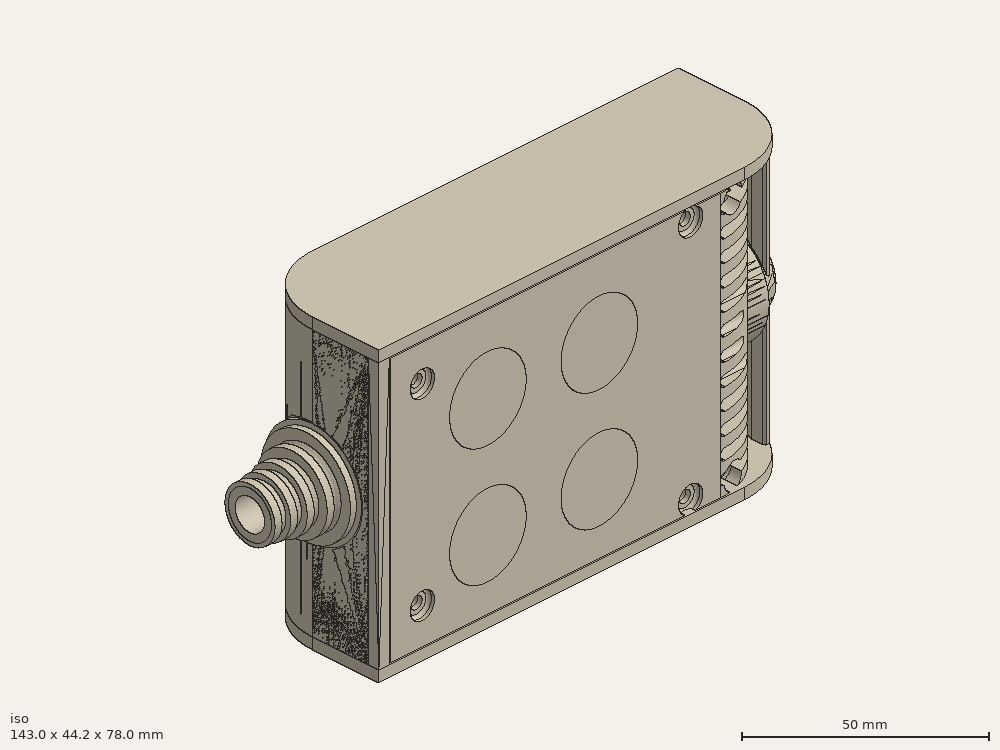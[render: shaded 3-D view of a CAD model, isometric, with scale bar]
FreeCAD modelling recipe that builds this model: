
FCSTD DOCUMENT  (FreeCAD 0.19R0.19.2)
Label: enclosure_128
License: All rights reserved
LicenseURL: http://en.wikipedia.org/wiki/All_rights_reserved
objects: Part::Feature×72, Part::Revolution×72, Part::MultiFuse×61, Sketcher::SketchObject×38, Part::Extrusion×26, Part::Fillet×26, Part::Cut×25, Part::Cylinder×22, Part::Box×12, App::MeasureDistance×4, Part::Chamfer×2
note: 356 computed .brp shape members not serialized (recipe doc carries the construction recipe); baked Part::Feature solids carry a one-line shape summary decoded from their .brp

FEATURE [Sketcher::SketchObject] Sketch  label="topSketch"
  FullyConstrained = true
  sketch-geometry (20):
    g0: LineSegment StartX=5.21097e-06 StartY=3 StartZ=0 EndX=5.21097e-06 EndY=19 EndZ=0
    g1: ArcOfCircle CenterX=19 CenterY=19 CenterZ=0 NormalX=0 NormalY=0 NormalZ=1 AngleXU=0 Radius=19 StartAngle=1.5708 EndAngle=3.14159
    g2: ArcOfCircle CenterX=19 CenterY=19 CenterZ=0 NormalX=0 NormalY=0 NormalZ=1 AngleXU=0 Radius=16 StartAngle=1.5708 EndAngle=3.14159
    g3: LineSegment StartX=114 StartY=35 StartZ=0 EndX=19 EndY=35 EndZ=0
    g4: LineSegment StartX=5.21097e-06 StartY=3 StartZ=0 EndX=5.21097e-06 EndY=0 EndZ=0
    g5: LineSegment StartX=3 StartY=0 StartZ=0 EndX=5.21097e-06 EndY=0 EndZ=0
    g6: LineSegment StartX=3 StartY=19 StartZ=0 EndX=3 EndY=0 EndZ=0
    g7: LineSegment StartX=19 StartY=38 StartZ=0 EndX=124 EndY=38 EndZ=0
    g8: Circle CenterX=119 CenterY=35 CenterZ=0 NormalX=0 NormalY=0 NormalZ=1 AngleXU=0 Radius=1
    g9: Circle CenterX=121 CenterY=35 CenterZ=0 NormalX=0 NormalY=0 NormalZ=1 AngleXU=0 Radius=1
    g10: Circle CenterX=121 CenterY=33 CenterZ=0 NormalX=0 NormalY=0 NormalZ=1 AngleXU=0 Radius=1
    g11: BSplineCurve PolesCount=3 KnotsCount=2 Degree=2 IsPeriodic=0
    g12: GeomPoint X=119 Y=35 Z=0
    g13: GeomPoint X=121 Y=33 Z=0
    g14: LineSegment StartX=119 StartY=35 StartZ=0 EndX=114 EndY=35 EndZ=0
    g15: ArcOfCircle CenterX=105 CenterY=19 CenterZ=0 NormalX=0 NormalY=0 NormalZ=1 AngleXU=0 Radius=19 StartAngle=5.7297 EndAngle=6.28319
    g16: ArcOfCircle CenterX=105 CenterY=19 CenterZ=0 NormalX=0 NormalY=0 NormalZ=1 AngleXU=0 Radius=16 StartAngle=5.60905 EndAngle=6.28319
    g17: LineSegment StartX=121 StartY=33 StartZ=0 EndX=121 EndY=19 EndZ=0
    g18: LineSegment StartX=124 StartY=38 StartZ=0 EndX=124 EndY=19 EndZ=0
    g19: LineSegment StartX=117.5 StartY=9.01251 StartZ=0 EndX=121.163 EndY=9.0125 EndZ=0
  constraints (46):
    c: Vertical(g0)
    c: Block(g0)
    c: Coincident(g1,g0)
    c: Block(g1)
    c: Coincident(g2,g1)
    c: Block(g2)
    c: Coincident(g3,g2)
    c: Horizontal(g3)
    c: Tangent(g3,g2)
    c: Coincident(g4,g0)
    c: Distance(g4) = 3
    c: Vertical(g4)
    c: Coincident(g5,g4)
    c: Horizontal(g5)
    c: Coincident(g6,g2)
    c: Coincident(g6,g5)
    c: Vertical(g6)
    c: Horizontal(g7)
    c: Distance(g7) = 105
    c: Coincident(g7,g1)
    c: Block(g3)
    c: Weight(g8) = 1
    c: Equal(g8,g9)
    c: Equal(g8,g10)
    c: InternalAlignment(g8,g11)
    c: InternalAlignment(g9,g11)
    c: InternalAlignment(g10,g11)
    c: InternalAlignment(g12,g11)
    c: InternalAlignment(g13,g11)
    c: Block(g11)
    c: Coincident(g14,g11)
    c: Coincident(g14,g3)
    c: Horizontal(g14)
    c: Block(g15)
    c: Coincident(g16,g15)
    c: Block(g16)
    c: Coincident(g17,g11)
    c: Coincident(g17,g16)
    c: Vertical(g17)
    c: Distance(g17) = 14
    c: Coincident(g18,g7)
    c: Coincident(g18,g15)
    c: Vertical(g18)
    c: Distance(g18) = 19
    c: Coincident(g19,g16)
    c: Coincident(g19,g15)
FEATURE [Sketcher::SketchObject] Sketch001  label="bottomSketch"
  FullyConstrained = true
  sketch-geometry (32):
    g0: LineSegment StartX=3.3 StartY=-6.03275e-07 StartZ=0 EndX=98 EndY=-6.03275e-07 EndZ=0
    g1: ArcOfCircle CenterX=98 CenterY=19 CenterZ=0 NormalX=0 NormalY=0 NormalZ=1 AngleXU=0 Radius=19 StartAngle=4.71239 EndAngle=5.71103
    g2: LineSegment StartX=6.3 StartY=8 StartZ=0 EndX=3.3 EndY=8 EndZ=0
    g3: LineSegment StartX=3.3 StartY=8 StartZ=0 EndX=3.3 EndY=-6.03275e-07 EndZ=0
    g4: ArcOfCircle CenterX=8.3 CenterY=5 CenterZ=0 NormalX=0 NormalY=0 NormalZ=1 AngleXU=0 Radius=2 StartAngle=3.14159 EndAngle=4.71239
    g5: LineSegment StartX=6.3 StartY=8 StartZ=0 EndX=6.3 EndY=5 EndZ=0
    g6: ArcOfCircle CenterX=98 CenterY=19 CenterZ=0 NormalX=0 NormalY=0 NormalZ=1 AngleXU=0 Radius=12.7 StartAngle=4.71239 EndAngle=6.28319
    g7: LineSegment StartX=94.7 StartY=3 StartZ=0 EndX=8.3 EndY=3 EndZ=0
    g8-g12: Circle x5 (B-spline internal-alignment scaffolding for g13; pole/knot coordinates omitted)
    g13: BSplineCurve PolesCount=5 KnotsCount=3 Degree=3 IsPeriodic=0
    g14: GeomPoint X=98 Y=6.3 Z=0
    g15: GeomPoint X=96.3938 Y=4.71946 Z=0
    g16: GeomPoint X=94.7 Y=3 Z=0
    g17-g23: Circle x7 (B-spline internal-alignment scaffolding for g24; pole/knot coordinates omitted)
    g24: BSplineCurve PolesCount=7 KnotsCount=5 Degree=3 IsPeriodic=0
    g25-g29: GeomPoint x5 (B-spline internal-alignment scaffolding for g24; pole/knot coordinates omitted)
    g30: ArcOfCircle CenterX=98 CenterY=19 CenterZ=0 NormalX=0 NormalY=0 NormalZ=1 AngleXU=0 Radius=15.7 StartAngle=5.81226 EndAngle=6.28319
    g31: LineSegment StartX=110.7 StartY=19 StartZ=0 EndX=113.7 EndY=19 EndZ=0
  constraints (41):
    c: Horizontal(g0)
    c: Coincident(g1,g0)
    c: Block(g1)
    c: Horizontal(g2)
    c: Distance(g2) = 3
    c: Coincident(g3,g2)
    c: Vertical(g3)
    c: Coincident(g3,g0)
    c: Block(g4)
    c: Block(g2)
    c: Coincident(g5,g2)
    c: Coincident(g5,g4)
    c: Vertical(g5)
    c: Coincident(g6,g1)
    c: Block(g6)
    c: Coincident(g7,g4)
    c: Horizontal(g7)
    c: Block(g0)
    c: Block(g7)
    c: Block(g3)
    c: Coincident(g13,g6)
    c: Weight(g8) = 1
    c: Equal(g8, g9-g12) x4
    c: Coincident(g13,g7)
    c: InternalAlignment(g8-g12 -> g13) x5
    c: InternalAlignment(g14,g13)
    c: InternalAlignment(g15,g13)
    c: InternalAlignment(g16,g13)
    c: Block(g13)
    c: Weight(g17) = 1
    c: Equal(g17, g18-g23) x6
    c: Coincident(g24,g1)
    c: InternalAlignment(g17-g23 -> g24) x7
    c: InternalAlignment(g25-g29 -> g24) x5
    c: Block(g24)
    c: Coincident(g30,g24)
    c: Coincident(g31,g6)
    c: Coincident(g31,g30)
    c: Horizontal(g31)
    c: Block(g31)
    c: Block(g30)
FEATURE [Part::Extrusion] Extrude  label="top"
  Base = -> Sketch
  Dir = (0,0,1)
  DirMode = 2
  FaceMakerClass = Part::FaceMakerBullseye
  LengthFwd = 72
  LengthRev = 0
  Solid = true
  Symmetric = false
FEATURE [Part::Extrusion] Extrude001  label="bottom"
  Base = -> Sketch001
  Dir = (0,0,1)
  DirMode = 2
  FaceMakerClass = Part::FaceMakerBullseye
  LengthFwd = 71.4
  LengthRev = 0
  Placement = pos=(0,0,0.3) rot=(0,0,1;0rad)
  Solid = true
  Symmetric = false
FEATURE [Sketcher::SketchObject] Sketch002  label="topSketch001"
  FullyConstrained = true
  sketch-geometry (6):
    g0: ArcOfCircle CenterX=19 CenterY=19 CenterZ=0 NormalX=0 NormalY=0 NormalZ=1 AngleXU=0 Radius=19 StartAngle=1.5708 EndAngle=3.14159
    g1: LineSegment StartX=5.22862e-06 StartY=19 StartZ=0 EndX=5.22862e-06 EndY=1.19904e-11 EndZ=0
    g2: LineSegment StartX=19 StartY=38 StartZ=0 EndX=124 EndY=38 EndZ=0
    g3: LineSegment StartX=5.22862e-06 StartY=1.19904e-11 StartZ=0 EndX=105 EndY=1.19904e-11 EndZ=0
    g4: ArcOfCircle CenterX=105 CenterY=19 CenterZ=0 NormalX=0 NormalY=0 NormalZ=1 AngleXU=0 Radius=19 StartAngle=4.71239 EndAngle=6.28319
    g5: LineSegment StartX=124 StartY=38 StartZ=0 EndX=124 EndY=19 EndZ=0
  constraints (16):
    c: Block(g0)
    c: Coincident(g1,g0)
    c: Vertical(g1)
    c: Horizontal(g2)
    c: Distance(g2) = 105
    c: Coincident(g2,g0)
    c: Distance(g1) = 19
    c: Coincident(g3,g1)
    c: Horizontal(g3)
    c: Distance(g3) = 105
    c: Block(g4)
    c: Coincident(g4,g3)
    c: Coincident(g5,g2)
    c: Coincident(g5,g4)
    c: Vertical(g5)
    c: Distance(g5) = 19
FEATURE [Part::Extrusion] Extrude002  label="sideA"
  Base = -> Sketch002
  Dir = (0,0,1)
  DirMode = 2
  FaceMakerClass = Part::FaceMakerBullseye
  LengthFwd = 3
  LengthRev = 0
  Placement = pos=(0,0,-3) rot=(0,0,1;0rad)
  Solid = true
  Symmetric = false
FEATURE [Sketcher::SketchObject] Sketch003  label="topSketch002"
  FullyConstrained = true
  sketch-geometry (6):
    g0: LineSegment StartX=19 StartY=38 StartZ=0 EndX=117 EndY=38 EndZ=0
    g1: ArcOfCircle CenterX=19 CenterY=19 CenterZ=0 NormalX=0 NormalY=0 NormalZ=1 AngleXU=0 Radius=19 StartAngle=1.5708 EndAngle=3.14159
    g2: LineSegment StartX=117 StartY=38 StartZ=0 EndX=117 EndY=19 EndZ=0
    g3: LineSegment StartX=98 StartY=1.0161e-12 StartZ=0 EndX=5.22862e-06 EndY=1.0161e-12 EndZ=0
    g4: LineSegment StartX=5.22862e-06 StartY=19 StartZ=0 EndX=5.22862e-06 EndY=1.0161e-12 EndZ=0
    g5: ArcOfCircle CenterX=98 CenterY=19 CenterZ=0 NormalX=0 NormalY=0 NormalZ=1 AngleXU=0 Radius=19 StartAngle=4.71239 EndAngle=6.28319
  constraints (16):
    c: Horizontal(g0)
    c: Distance(g0) = 98
    c: Coincident(g1,g0)
    c: Block(g1)
    c: Coincident(g2,g0)
    c: Vertical(g2)
    c: Distance(g2) = 19
    c: Horizontal(g3)
    c: Coincident(g4,g1)
    c: Vertical(g4)
    c: Coincident(g3,g4)
    c: Block(g3)
    c: Coincident(g5,g2)
    c: Coincident(g5,g3)
    c: Block(g0)
    c: Block(g5)
FEATURE [Sketcher::SketchObject] Sketch004
  FullyConstrained = true
  MapMode = 3
  Placement = pos=(0,0,0) rot=(1,0,0;1.5708rad)
  Support = -> [Extrude]
  sketch-geometry (8):
    g0: Circle CenterX=80.351 CenterY=-67.6202 CenterZ=0 NormalX=0 NormalY=0 NormalZ=1 AngleXU=0 Radius=2
    g1: Circle CenterX=80.351 CenterY=-67.6202 CenterZ=0 NormalX=0 NormalY=0 NormalZ=1 AngleXU=0 Radius=3
    g2: Circle CenterX=80.351 CenterY=-4.92017 CenterZ=0 NormalX=0 NormalY=0 NormalZ=1 AngleXU=0 Radius=2
    g3: Circle CenterX=80.351 CenterY=-4.92017 CenterZ=0 NormalX=0 NormalY=0 NormalZ=1 AngleXU=0 Radius=3
    g4: Circle CenterX=23.851 CenterY=-4.92017 CenterZ=0 NormalX=0 NormalY=0 NormalZ=1 AngleXU=0 Radius=2
    g5: Circle CenterX=23.851 CenterY=-4.92017 CenterZ=0 NormalX=0 NormalY=0 NormalZ=1 AngleXU=0 Radius=3
    g6: Circle CenterX=23.851 CenterY=-67.6202 CenterZ=0 NormalX=0 NormalY=0 NormalZ=1 AngleXU=0 Radius=2
    g7: Circle CenterX=23.851 CenterY=-67.6202 CenterZ=0 NormalX=0 NormalY=0 NormalZ=1 AngleXU=0 Radius=3
  constraints (8):
    c: Block(g3)
    c: Block(g2)
    c: Block(g1)
    c: Block(g0)
    c: Block(g6)
    c: Block(g7)
    c: Block(g4)
    c: Block(g5)
FEATURE [Part::Extrusion] Extrude004
  Base = -> Sketch004
  Dir = (0,-1,2e-16)
  DirMode = 2
  FaceMakerClass = Part::FaceMakerBullseye
  LengthFwd = 6
  LengthRev = 0
  Placement = pos=(0,9,0) rot=(0,0,1;0rad)
  Solid = true
  Symmetric = false
FEATURE [Sketcher::SketchObject] Sketch005
  FullyConstrained = true
  MapMode = 3
  Placement = pos=(0,0,0) rot=(1,0,0;1.5708rad)
  Support = -> [Extrude]
  sketch-geometry (8):
    g0: Circle CenterX=80.351 CenterY=-67.6202 CenterZ=0 NormalX=0 NormalY=0 NormalZ=1 AngleXU=0 Radius=3
    g1: Circle CenterX=80.351 CenterY=-4.92017 CenterZ=0 NormalX=0 NormalY=0 NormalZ=1 AngleXU=0 Radius=3
    g2: Circle CenterX=23.851 CenterY=-4.92017 CenterZ=0 NormalX=0 NormalY=0 NormalZ=1 AngleXU=0 Radius=3
    g3: Circle CenterX=23.851 CenterY=-67.6202 CenterZ=0 NormalX=0 NormalY=0 NormalZ=1 AngleXU=0 Radius=3
    g4: Circle CenterX=23.851 CenterY=-67.6202 CenterZ=0 NormalX=0 NormalY=0 NormalZ=1 AngleXU=0 Radius=5
    g5: Circle CenterX=80.351 CenterY=-67.6202 CenterZ=0 NormalX=0 NormalY=0 NormalZ=1 AngleXU=0 Radius=5
    g6: Circle CenterX=23.851 CenterY=-4.92017 CenterZ=0 NormalX=0 NormalY=0 NormalZ=1 AngleXU=0 Radius=5
    g7: Circle CenterX=80.351 CenterY=-4.92017 CenterZ=0 NormalX=0 NormalY=0 NormalZ=1 AngleXU=0 Radius=5
  constraints (8):
    c: Block(g1)
    c: Block(g0)
    c: Block(g3)
    c: Block(g2)
    c: Block(g5)
    c: Block(g4)
    c: Block(g6)
    c: Block(g7)
FEATURE [Part::Extrusion] Extrude005
  Base = -> Sketch005
  Dir = (0,-1,2e-16)
  DirMode = 2
  FaceMakerClass = Part::FaceMakerBullseye
  LengthFwd = 2
  LengthRev = 0
  Solid = true
  Symmetric = false
FEATURE [Sketcher::SketchObject] Sketch006
  FullyConstrained = true
  MapMode = 3
  Placement = pos=(0,0,0) rot=(1,0,0;1.5708rad)
  sketch-geometry (8):
    g0: Circle CenterX=80.351 CenterY=-67.6202 CenterZ=0 NormalX=0 NormalY=0 NormalZ=1 AngleXU=0 Radius=3
    g1: Circle CenterX=80.351 CenterY=-4.92017 CenterZ=0 NormalX=0 NormalY=0 NormalZ=1 AngleXU=0 Radius=3
    g2: Circle CenterX=23.851 CenterY=-4.92017 CenterZ=0 NormalX=0 NormalY=0 NormalZ=1 AngleXU=0 Radius=3
    g3: Circle CenterX=23.851 CenterY=-67.6202 CenterZ=0 NormalX=0 NormalY=0 NormalZ=1 AngleXU=0 Radius=3
    g4: Circle CenterX=23.851 CenterY=-67.6202 CenterZ=0 NormalX=0 NormalY=0 NormalZ=1 AngleXU=0 Radius=5
    g5: Circle CenterX=80.351 CenterY=-67.6202 CenterZ=0 NormalX=0 NormalY=0 NormalZ=1 AngleXU=0 Radius=5
    g6: Circle CenterX=23.851 CenterY=-4.92017 CenterZ=0 NormalX=0 NormalY=0 NormalZ=1 AngleXU=0 Radius=5
    g7: Circle CenterX=80.351 CenterY=-4.92017 CenterZ=0 NormalX=0 NormalY=0 NormalZ=1 AngleXU=0 Radius=5
  constraints (8):
    c: Block(g1)
    c: Block(g0)
    c: Block(g3)
    c: Block(g2)
    c: Block(g5)
    c: Block(g4)
    c: Block(g6)
    c: Block(g7)
FEATURE [Part::Extrusion] Extrude007
  Base = -> Sketch006
  Dir = (0,-1,2e-16)
  DirMode = 2
  FaceMakerClass = Part::FaceMakerBullseye
  LengthFwd = 2
  LengthRev = 0
  Solid = true
  Symmetric = false
FEATURE [Part::Fillet] Fillet
  Base = -> Extrude007
  Edges = 4 edges r=1.99: [Edge6,Edge12,Edge18,Edge24]
FEATURE [Part::Cut] Cut
  Base = -> Extrude005
  Placement = pos=(0,5,0) rot=(0,0,1;0rad)
  Tool = -> Fillet
FEATURE [Part::MultiFuse] Fusion  label="pCBScrews"
  Placement = pos=(-2.5,0,72.3) rot=(0,0,1;0rad)
  Shapes = -> [Extrude004,Cut]
FEATURE [App::MeasureDistance] Distance  label="Distance: 0.69 mm"
  Distance = 0.685967
  P1 = (24.0138,2.9647,0.3)
  P2 = (23.8901,3,-0.373787)
FEATURE [App::MeasureDistance] Distance001  label="Distance: 0.53 mm"
  Distance = 0.533607
  P1 = (80.2939,3,72.2334)
  P2 = (80.281,2.99661,71.7)
FEATURE [Part::Fillet] Fillet001
  Base = -> Extrude001
  Edges = 1 edges r=2.4: [Edge17]
FEATURE [Part::Fillet] Fillet002  label="bottom001"
  Base = -> Fillet001
  Edges = 1 edges r=2.4: [Edge36]
FEATURE [Part::Fillet] Fillet003  label="top001"
  Base = -> Extrude
  Edges = 1 edges r=2: [Edge1]
FEATURE [Sketcher::SketchObject] Sketch007
  FullyConstrained = true
  sketch-geometry (16):
    g0: LineSegment StartX=4 StartY=0 StartZ=0 EndX=4 EndY=2.4 EndZ=0
    g1: LineSegment StartX=4 StartY=2.4 StartZ=0 EndX=7 EndY=2.4 EndZ=0
    g2: LineSegment StartX=4 StartY=0 StartZ=0 EndX=5.7 EndY=0 EndZ=0
    g3: LineSegment StartX=5.7 StartY=0 StartZ=0 EndX=5.7 EndY=-5.6 EndZ=0
    g4-g8: Circle x5 (B-spline internal-alignment scaffolding for g9; pole/knot coordinates omitted)
    g9: BSplineCurve PolesCount=5 KnotsCount=3 Degree=3 IsPeriodic=0
    g10: GeomPoint X=7 Y=2.4 Z=0
    g11: GeomPoint X=10.4582 Y=-1.55472 Z=0
    g12: GeomPoint X=14 Y=-5.6 Z=0
    g13: LineSegment StartX=14 StartY=-5.6 StartZ=0 EndX=14 EndY=-14.1 EndZ=0
    g14: LineSegment StartX=14 StartY=-14.1 StartZ=0 EndX=6.5 EndY=-14.1 EndZ=0
    g15: LineSegment StartX=5.7 StartY=-5.6 StartZ=0 EndX=6.5 EndY=-14.1 EndZ=0
  constraints (28):
    c: Distance(g0) = 2.4
    c: Vertical(g0)
    c: Block(g0)
    c: Coincident(g1,g0)
    c: Horizontal(g1)
    c: Distance(g1) = 3
    c: Coincident(g2,g0)
    c: Horizontal(g2)
    c: Distance(g2) = 1.7
    c: Coincident(g3,g2)
    c: Vertical(g3)
    c: Distance(g3) = 5.6
    c: Coincident(g9,g1)
    c: Weight(g4) = 1
    c: Equal(g4, g5-g8) x4
    c: InternalAlignment(g4-g8 -> g9) x5
    c: InternalAlignment(g10,g9)
    c: InternalAlignment(g11,g9)
    c: InternalAlignment(g12,g9)
    c: Block(g9)
    c: Coincident(g13,g9)
    c: Vertical(g13)
    c: Distance(g13) = 8.5
    c: Coincident(g14,g13)
    c: Horizontal(g14)
    c: Distance(g14) = 7.5
    c: Coincident(g15,g3)
    c: Coincident(g15,g14)
FEATURE [Part::Feature] Face
  shape: bbox 10 x 16.5 x 2e-07 mm, 1 faces, 0 solids (baked)
FEATURE [Part::Revolution] Revolve  label="plugHousing"
  Angle = 360
  Axis = (0,1,0)
  Base = (0,0,0)
  FaceMakerClass = Part::FaceMakerBullseye
  Placement = pos=(0,0,36.15) rot=(0,0,1;0rad)
  Solid = false
  Source = -> Face
  Symmetric = false
FEATURE [Part::Feature] Face001
  shape: bbox 10 x 16.5 x 2e-07 mm, 1 faces, 0 solids (baked)
FEATURE [Part::Revolution] Revolve001  label="plugHousing001"
  Angle = 360
  Axis = (0,1,0)
  Base = (0,0,0)
  FaceMakerClass = Part::FaceMakerBullseye
  Placement = pos=(0,0,36.15) rot=(0,0,1;0rad)
  Solid = false
  Source = -> Face001
  Symmetric = false
FEATURE [Part::MultiFuse] Fusion001  label="plugHousing002"
  Placement = pos=(0,0,0) rot=(0,0,1;1.5708rad)
  Shapes = -> [Revolve001,Revolve]
FEATURE [Part::Feature] Face002
  shape: bbox 10 x 16.5 x 2e-07 mm, 1 faces, 0 solids (baked)
FEATURE [Part::Revolution] Revolve003  label="plugHousing005"
  Angle = 360
  Axis = (0,1,0)
  Base = (0,0,0)
  FaceMakerClass = Part::FaceMakerBullseye
  Placement = pos=(0,0,36.15) rot=(0,0,1;0rad)
  Solid = false
  Source = -> Face002
  Symmetric = false
FEATURE [Part::Feature] Face003
  shape: bbox 10 x 16.5 x 2e-07 mm, 1 faces, 0 solids (baked)
FEATURE [Part::Revolution] Revolve002  label="plugHousing003"
  Angle = 360
  Axis = (0,1,0)
  Base = (0,0,0)
  FaceMakerClass = Part::FaceMakerBullseye
  Placement = pos=(0,0,36.15) rot=(0,0,1;0rad)
  Solid = false
  Source = -> Face003
  Symmetric = false
FEATURE [Part::MultiFuse] Fusion002  label="plugHousing004"
  Placement = pos=(0,0,0) rot=(0,0,1;1.5708rad)
  Shapes = -> [Revolve002,Revolve003]
FEATURE [Part::MultiFuse] Fusion003  label="plugHousing006"
  Placement = pos=(0,19,0) rot=(0,0,1;3.14159rad)
  Shapes = -> [Fusion002,Fusion001]
FEATURE [Part::Feature] Face004
  shape: bbox 10 x 16.5 x 2e-07 mm, 1 faces, 0 solids (baked)
FEATURE [Part::Revolution] Revolve006  label="plugHousing010"
  Angle = 360
  Axis = (0,1,0)
  Base = (0,0,0)
  FaceMakerClass = Part::FaceMakerBullseye
  Placement = pos=(0,0,36.15) rot=(0,0,1;0rad)
  Solid = false
  Source = -> Face004
  Symmetric = false
FEATURE [Part::Feature] Face005
  shape: bbox 10 x 16.5 x 2e-07 mm, 1 faces, 0 solids (baked)
FEATURE [Part::Revolution] Revolve007  label="plugHousing011"
  Angle = 360
  Axis = (0,1,0)
  Base = (0,0,0)
  FaceMakerClass = Part::FaceMakerBullseye
  Placement = pos=(0,0,36.15) rot=(0,0,1;0rad)
  Solid = false
  Source = -> Face005
  Symmetric = false
FEATURE [Part::Feature] Face006
  shape: bbox 10 x 16.5 x 2e-07 mm, 1 faces, 0 solids (baked)
FEATURE [Part::Revolution] Revolve004  label="plugHousing007"
  Angle = 360
  Axis = (0,1,0)
  Base = (0,0,0)
  FaceMakerClass = Part::FaceMakerBullseye
  Placement = pos=(0,0,36.15) rot=(0,0,1;0rad)
  Solid = false
  Source = -> Face006
  Symmetric = false
FEATURE [Part::MultiFuse] Fusion004  label="plugHousing009"
  Placement = pos=(0,0,0) rot=(0,0,1;1.5708rad)
  Shapes = -> [Revolve004,Revolve007]
FEATURE [Part::Feature] Face007
  shape: bbox 10 x 16.5 x 2e-07 mm, 1 faces, 0 solids (baked)
FEATURE [Part::Revolution] Revolve005  label="plugHousing008"
  Angle = 360
  Axis = (0,1,0)
  Base = (0,0,0)
  FaceMakerClass = Part::FaceMakerBullseye
  Placement = pos=(0,0,36.15) rot=(0,0,1;0rad)
  Solid = false
  Source = -> Face007
  Symmetric = false
FEATURE [Part::MultiFuse] Fusion005  label="plugHousing012"
  Placement = pos=(0,0,0) rot=(0,0,1;1.5708rad)
  Shapes = -> [Revolve006,Revolve005]
FEATURE [Part::MultiFuse] Fusion006  label="plugHousing013"
  Placement = pos=(0,19,0) rot=(0,0,1;3.14159rad)
  Shapes = -> [Fusion005,Fusion004]
FEATURE [Part::MultiFuse] Fusion007  label="plugHousing014"
  Placement = pos=(122.621,0,-0.15) rot=(0,0,1;0rad)
  Shapes = -> [Fusion003,Fusion006]
FEATURE [Part::Cylinder] Cylinder002
  Angle = 360
  AttacherType = Attacher::AttachEngine3D
  Height = 20
  Placement = pos=(0,0,36.15) rot=(0,0,1;0rad)
  Radius = 4
FEATURE [Part::Cylinder] Cylinder003
  Angle = 360
  AttacherType = Attacher::AttachEngine3D
  Height = 10
  Placement = pos=(0,0,36.15) rot=(0,0,1;0rad)
  Radius = 4
FEATURE [Part::MultiFuse] Fusion009  label="removeToCreateHoleForPlugHousing"
  Placement = pos=(70,19,36.15) rot=(0,1,0;1.5708rad)
  Shapes = -> [Cylinder002,Cylinder003]
FEATURE [Part::Cylinder] Cylinder004
  Angle = 360
  AttacherType = Attacher::AttachEngine3D
  Height = 20
  Placement = pos=(0,0,36.15) rot=(0,0,1;0rad)
  Radius = 4
FEATURE [Part::Cylinder] Cylinder005
  Angle = 360
  AttacherType = Attacher::AttachEngine3D
  Height = 10
  Placement = pos=(0,0,36.15) rot=(0,0,1;0rad)
  Radius = 4
FEATURE [Part::MultiFuse] Fusion010  label="removeToCreateHoleForPlugHousing001"
  Placement = pos=(70,19,36.15) rot=(0,1,0;1.5708rad)
  Shapes = -> [Cylinder004,Cylinder005]
FEATURE [Part::Cut] Cut001
  Base = -> Fillet003
  Tool = -> Fusion010
FEATURE [Part::Cut] Cut002  label="Bottom"
  Base = -> Fillet002
  Tool = -> Fusion009
FEATURE [Part::Feature] Face008
  shape: bbox 10 x 16.5 x 2e-07 mm, 1 faces, 0 solids (baked)
FEATURE [Part::Revolution] Revolve011  label="plugHousing021"
  Angle = 360
  Axis = (0,1,0)
  Base = (0,0,0)
  FaceMakerClass = Part::FaceMakerBullseye
  Placement = pos=(0,0,36.15) rot=(0,0,1;0rad)
  Solid = false
  Source = -> Face008
  Symmetric = false
FEATURE [Part::Feature] Face009
  shape: bbox 10 x 16.5 x 2e-07 mm, 1 faces, 0 solids (baked)
FEATURE [Part::Revolution] Revolve012  label="plugHousing022"
  Angle = 360
  Axis = (0,1,0)
  Base = (0,0,0)
  FaceMakerClass = Part::FaceMakerBullseye
  Placement = pos=(0,0,36.15) rot=(0,0,1;0rad)
  Solid = false
  Source = -> Face009
  Symmetric = false
FEATURE [Part::Feature] Face010 .. Face013  x4 (patterned run collapsed; names and placements below)
  shape: bbox 10 x 16.5 x 2e-07 mm, 1 faces, 0 solids (baked)
FEATURE [Part::Revolution] Revolve015  label="plugHousing027"
  Angle = 360
  Axis = (0,1,0)
  Base = (0,0,0)
  FaceMakerClass = Part::FaceMakerBullseye
  Placement = pos=(0,0,36.15) rot=(0,0,1;0rad)
  Solid = false
  Source = -> Face013
  Symmetric = false
FEATURE [Part::Feature] Face014
  shape: bbox 10 x 16.5 x 2e-07 mm, 1 faces, 0 solids (baked)
FEATURE [Part::Feature] Face015
  shape: bbox 10 x 16.5 x 2e-07 mm, 1 faces, 0 solids (baked)
FEATURE [Part::Feature] Face016
  shape: bbox 10 x 16.5 x 2e-07 mm, 1 faces, 0 solids (baked)
FEATURE [Part::Revolution] Revolve019  label="plugHousing033"
  Angle = 360
  Axis = (0,1,0)
  Base = (0,0,0)
  FaceMakerClass = Part::FaceMakerBullseye
  Placement = pos=(0,0,36.15) rot=(0,0,1;0rad)
  Solid = false
  Source = -> Face016
  Symmetric = false
FEATURE [Part::Feature] Face017
  shape: bbox 10 x 16.5 x 2e-07 mm, 1 faces, 0 solids (baked)
FEATURE [Part::Revolution] Revolve020  label="plugHousing034"
  Angle = 360
  Axis = (0,1,0)
  Base = (0,0,0)
  FaceMakerClass = Part::FaceMakerBullseye
  Placement = pos=(0,0,36.15) rot=(0,0,1;0rad)
  Solid = false
  Source = -> Face017
  Symmetric = false
FEATURE [Part::Feature] Face018
  shape: bbox 10 x 16.5 x 2e-07 mm, 1 faces, 0 solids (baked)
FEATURE [Part::Revolution] Revolve016  label="plugHousing030"
  Angle = 360
  Axis = (0,1,0)
  Base = (0,0,0)
  FaceMakerClass = Part::FaceMakerBullseye
  Placement = pos=(0,0,36.15) rot=(0,0,1;0rad)
  Solid = false
  Source = -> Face018
  Symmetric = false
FEATURE [Part::MultiFuse] Fusion020  label="plugHousing038"
  Placement = pos=(0,0,0) rot=(0,0,1;1.5708rad)
  Shapes = -> [Revolve016,Revolve020]
FEATURE [Part::Feature] Face019
  shape: bbox 10 x 16.5 x 2e-07 mm, 1 faces, 0 solids (baked)
FEATURE [Part::Feature] Face020
  shape: bbox 10 x 16.5 x 2e-07 mm, 1 faces, 0 solids (baked)
FEATURE [Part::Revolution] Revolve017  label="plugHousing031"
  Angle = 360
  Axis = (0,1,0)
  Base = (0,0,0)
  FaceMakerClass = Part::FaceMakerBullseye
  Placement = pos=(0,0,36.15) rot=(0,0,1;0rad)
  Solid = false
  Source = -> Face020
  Symmetric = false
FEATURE [Part::MultiFuse] Fusion021  label="plugHousing039"
  Placement = pos=(0,0,0) rot=(0,0,1;1.5708rad)
  Shapes = -> [Revolve019,Revolve017]
FEATURE [Part::MultiFuse] Fusion023  label="plugHousing041"
  Placement = pos=(0,19,0) rot=(0,0,1;3.14159rad)
  Shapes = -> [Fusion021,Fusion020]
FEATURE [Part::Revolution] Revolve022  label="plugHousing043"
  Angle = 360
  Axis = (0,1,0)
  Base = (0,0,0)
  FaceMakerClass = Part::FaceMakerBullseye
  Placement = pos=(0,0,36.15) rot=(0,0,1;0rad)
  Solid = false
  Source = -> Face019
  Symmetric = false
FEATURE [Part::Feature] Face021
  shape: bbox 10 x 16.5 x 2e-07 mm, 1 faces, 0 solids (baked)
FEATURE [Part::Revolution] Revolve023  label="plugHousing044"
  Angle = 360
  Axis = (0,1,0)
  Base = (0,0,0)
  FaceMakerClass = Part::FaceMakerBullseye
  Placement = pos=(0,0,36.15) rot=(0,0,1;0rad)
  Solid = false
  Source = -> Face021
  Symmetric = false
FEATURE [Part::Feature] Face022
  shape: bbox 10 x 16.5 x 2e-07 mm, 1 faces, 0 solids (baked)
FEATURE [Part::Revolution] Revolve018  label="plugHousing032"
  Angle = 360
  Axis = (0,1,0)
  Base = (0,0,0)
  FaceMakerClass = Part::FaceMakerBullseye
  Placement = pos=(0,0,36.15) rot=(0,0,1;0rad)
  Solid = false
  Source = -> Face022
  Symmetric = false
FEATURE [Part::MultiFuse] Fusion022  label="plugHousing040"
  Placement = pos=(0,0,0) rot=(0,0,1;1.5708rad)
  Shapes = -> [Revolve018,Revolve023]
FEATURE [Part::Feature] Face023
  shape: bbox 10 x 16.5 x 2e-07 mm, 1 faces, 0 solids (baked)
FEATURE [Part::Revolution] Revolve021  label="plugHousing035"
  Angle = 360
  Axis = (0,1,0)
  Base = (0,0,0)
  FaceMakerClass = Part::FaceMakerBullseye
  Placement = pos=(0,0,36.15) rot=(0,0,1;0rad)
  Solid = false
  Source = -> Face023
  Symmetric = false
FEATURE [Part::MultiFuse] Fusion018  label="plugHousing036"
  Placement = pos=(0,0,0) rot=(0,0,1;1.5708rad)
  Shapes = -> [Revolve022,Revolve021]
FEATURE [Part::MultiFuse] Fusion019  label="plugHousing037"
  Placement = pos=(0,19,0) rot=(0,0,1;3.14159rad)
  Shapes = -> [Fusion018,Fusion022]
FEATURE [Part::MultiFuse] Fusion024  label="plugHousing042"
  Placement = pos=(122.621,0,-0.15) rot=(0,0,1;0rad)
  Shapes = -> [Fusion023,Fusion019]
FEATURE [Part::Cylinder] Cylinder006
  Angle = 360
  AttacherType = Attacher::AttachEngine3D
  Height = 20
  Placement = pos=(0,0,36.15) rot=(0,0,1;0rad)
  Radius = 14.3
FEATURE [Part::Cylinder] Cylinder007
  Angle = 360
  AttacherType = Attacher::AttachEngine3D
  Height = 10
  Placement = pos=(0,0,36.15) rot=(0,0,1;0rad)
  Radius = 4
FEATURE [Part::MultiFuse] Fusion026  label="removeToCreteHoleForPlugHousing"
  Placement = pos=(70,19,36) rot=(0,1,0;1.5708rad)
  Shapes = -> [Cylinder006,Cylinder007]
FEATURE [Part::Box] Box001  label="Cube001"
  AttacherType = Attacher::AttachEngine3D
  Height = 28
  Length = 3
  Placement = pos=(110.7,19,22) rot=(0,0,1;0rad)
  Width = 15.7
FEATURE [Part::Cut] Cut003  label="top002"
  Base = -> Cut001
  Tool = -> Fusion007
FEATURE [Part::Revolution] Revolve008  label="plugHousing015"
  Angle = 360
  Axis = (0,1,0)
  Base = (0,0,0)
  FaceMakerClass = Part::FaceMakerBullseye
  Placement = pos=(0,0,36.15) rot=(0,0,1;0rad)
  Solid = false
  Source = -> Face010
  Symmetric = false
FEATURE [Part::MultiFuse] Fusion013  label="plugHousing020"
  Placement = pos=(0,0,0) rot=(0,0,1;1.5708rad)
  Shapes = -> [Revolve008,Revolve012]
FEATURE [Part::Cut] Cut004  label="top003"
  Base = -> Cut003
  Placement = pos=(1,0,0) rot=(0,0,1;0rad)
  Tool = -> Fusion026
FEATURE [Part::Cylinder] Cylinder008
  Angle = 360
  AttacherType = Attacher::AttachEngine3D
  Height = 20
  Placement = pos=(0,0,36.15) rot=(0,0,1;0rad)
  Radius = 10.3
FEATURE [Part::Cylinder] Cylinder009
  Angle = 360
  AttacherType = Attacher::AttachEngine3D
  Height = 10
  Placement = pos=(0,0,36.15) rot=(0,0,1;0rad)
  Radius = 4
FEATURE [Part::MultiFuse] Fusion027  label="removeToCreteHoleForPlugHousing001"
  Placement = pos=(70,19,36) rot=(0,1,0;1.5708rad)
  Shapes = -> [Cylinder008,Cylinder009]
FEATURE [Part::Cut] Cut005  label="plugHousingTab"
  Base = -> Box001
  Tool = -> Fusion027
FEATURE [Part::MultiFuse] Fusion028  label="plugHousing045"
  Shapes = -> [Fusion024,Cut005]
FEATURE [Part::Box] Box002  label="Cube002"
  AttacherType = Attacher::AttachEngine3D
  Height = 28.8
  Length = 3
  Placement = pos=(107.3,28,21.6) rot=(0,0,1;0rad)
  Width = 7
FEATURE [Part::Box] Box003  label="Cube003"
  AttacherType = Attacher::AttachEngine3D
  Height = 3
  Length = 6.4
  Placement = pos=(107.3,28,18.6) rot=(0,0,1;0rad)
  Width = 7
FEATURE [Part::Box] Box004  label="Cube004"
  AttacherType = Attacher::AttachEngine3D
  Height = 3
  Length = 6.4
  Placement = pos=(107.3,28,50.4) rot=(0,0,1;0rad)
  Width = 7
FEATURE [Part::MultiFuse] Fusion029  label="plugHousingBracketHolder"
  Shapes = -> [Box004,Box002,Box003]
FEATURE [Part::Cylinder] Cylinder010
  Angle = 360
  AttacherType = Attacher::AttachEngine3D
  Height = 20
  Placement = pos=(0,0,36.15) rot=(0,0,1;0rad)
  Radius = 14.3
FEATURE [Part::Cylinder] Cylinder011
  Angle = 360
  AttacherType = Attacher::AttachEngine3D
  Height = 10
  Placement = pos=(0,0,36.15) rot=(0,0,1;0rad)
  Radius = 4
FEATURE [Part::MultiFuse] Fusion030  label="removeToCreteHoleForPlugHousing002"
  Placement = pos=(70,19,36) rot=(0,1,0;1.5708rad)
  Shapes = -> [Cylinder010,Cylinder011]
FEATURE [Part::Cut] Cut006  label="plugHousingBracketHolder001"
  Base = -> Fusion029
  Tool = -> Fusion030
FEATURE [Part::Cylinder] Cylinder012
  Angle = 360
  AttacherType = Attacher::AttachEngine3D
  Height = 20
  Placement = pos=(0,0,36.15) rot=(0,0,1;0rad)
  Radius = 7
FEATURE [Part::Cylinder] Cylinder013
  Angle = 360
  AttacherType = Attacher::AttachEngine3D
  Height = 10
  Placement = pos=(0,0,36.15) rot=(0,0,1;0rad)
  Radius = 4
FEATURE [Part::MultiFuse] Fusion032  label="removeToCreteHoleForPlugHousing003"
  Placement = pos=(70,19,36) rot=(0,1,0;1.5708rad)
  Shapes = -> [Cylinder012,Cylinder013]
FEATURE [Part::Cut] Cut007  label="bottom002"
  Base = -> Cut002
  Tool = -> Fusion032
FEATURE [Sketcher::SketchObject] Sketch008
  FullyConstrained = true
  sketch-geometry (54):
    g0: LineSegment StartX=-4.2 StartY=0 StartZ=0 EndX=-6.2 EndY=0 EndZ=0
    g1: LineSegment StartX=-14 StartY=-18 StartZ=0 EndX=-14 EndY=-26.5 EndZ=0
    g2: LineSegment StartX=-4.2 StartY=0 StartZ=0 EndX=-4.2 EndY=-13.4877 EndZ=0
    g3: Circle CenterX=-4.2 CenterY=-13.4877 CenterZ=0 NormalX=0 NormalY=0 NormalZ=1 AngleXU=0 Radius=1
    g4: Circle CenterX=-4.2 CenterY=-26.5 CenterZ=0 NormalX=0 NormalY=0 NormalZ=1 AngleXU=0 Radius=1
    g5: Circle CenterX=-8.2 CenterY=-26.5 CenterZ=0 NormalX=0 NormalY=0 NormalZ=1 AngleXU=0 Radius=1
    g6: BSplineCurve PolesCount=3 KnotsCount=2 Degree=2 IsPeriodic=0
    g7: GeomPoint X=-4.2 Y=-13.4877 Z=0
    g8: GeomPoint X=-8.2 Y=-26.5 Z=0
    g9: LineSegment StartX=-14 StartY=-26.5 StartZ=0 EndX=-8.2 EndY=-26.5 EndZ=0
    g10: LineSegment StartX=-10.15 StartY=-12 StartZ=0 EndX=-10.15 EndY=-14 EndZ=0
    g11: LineSegment StartX=-12.8401 StartY=-16 StartZ=0 EndX=-10.1571 EndY=-16 EndZ=0
    g12: LineSegment StartX=-10.15 StartY=-14 StartZ=0 EndX=-8.70761 EndY=-14 EndZ=0
    g13: LineSegment StartX=-12.8401 StartY=-16 StartZ=0 EndX=-12.8401 EndY=-17.6958 EndZ=0
    g14: LineSegment StartX=-10.15 StartY=-12 StartZ=0 EndX=-7.79258 EndY=-12 EndZ=0
    g15: Circle CenterX=-6.2215 CenterY=-2 CenterZ=0 NormalX=0 NormalY=0 NormalZ=1 AngleXU=0 Radius=1
    g16: Circle CenterX=-6.22762 CenterY=-2.58724 CenterZ=0 NormalX=0 NormalY=0 NormalZ=1 AngleXU=0 Radius=1
    g17: Circle CenterX=-6.32538 CenterY=-4 CenterZ=0 NormalX=0 NormalY=0 NormalZ=1 AngleXU=0 Radius=1
    g18: BSplineCurve PolesCount=3 KnotsCount=2 Degree=2 IsPeriodic=0
    g19: GeomPoint X=-6.2215 Y=-2 Z=0
    g20: GeomPoint X=-6.32538 Y=-4 Z=0
    g21: Circle CenterX=-6.48644 CenterY=-5.99526 CenterZ=0 NormalX=0 NormalY=0 NormalZ=1 AngleXU=0 Radius=1
    g22: Circle CenterX=-6.58486 CenterY=-6.99526 CenterZ=0 NormalX=0 NormalY=0 NormalZ=1 AngleXU=0 Radius=1
    g23: Circle CenterX=-6.77343 CenterY=-8 CenterZ=0 NormalX=0 NormalY=0 NormalZ=1 AngleXU=0 Radius=1
    g24: BSplineCurve PolesCount=3 KnotsCount=2 Degree=2 IsPeriodic=0
    g25: GeomPoint X=-6.48644 Y=-5.99526 Z=0
    g26: GeomPoint X=-6.77343 Y=-8 Z=0
    g27: Circle CenterX=-7.19003 CenterY=-10 CenterZ=0 NormalX=0 NormalY=0 NormalZ=1 AngleXU=0 Radius=1
    g28: Circle CenterX=-7.44407 CenterY=-11.0915 CenterZ=0 NormalX=0 NormalY=0 NormalZ=1 AngleXU=0 Radius=1
    g29: Circle CenterX=-7.79258 CenterY=-12 CenterZ=0 NormalX=0 NormalY=0 NormalZ=1 AngleXU=0 Radius=1
    g30: BSplineCurve PolesCount=3 KnotsCount=2 Degree=2 IsPeriodic=0
    g31: GeomPoint X=-7.19003 Y=-10 Z=0
    g32: GeomPoint X=-7.79258 Y=-12 Z=0
    g33: Circle CenterX=-8.70761 CenterY=-14 CenterZ=0 NormalX=0 NormalY=0 NormalZ=1 AngleXU=0 Radius=1
    g34: Circle CenterX=-9.33087 CenterY=-15.1837 CenterZ=0 NormalX=0 NormalY=0 NormalZ=1 AngleXU=0 Radius=1
    g35: Circle CenterX=-10.1571 CenterY=-16 CenterZ=0 NormalX=0 NormalY=0 NormalZ=1 AngleXU=0 Radius=1
    g36: BSplineCurve PolesCount=3 KnotsCount=2 Degree=2 IsPeriodic=0
    g37: GeomPoint X=-8.70761 Y=-14 Z=0
    g38: GeomPoint X=-10.1571 Y=-16 Z=0
    g39: Circle CenterX=-12.8401 CenterY=-17.6958 CenterZ=0 NormalX=0 NormalY=0 NormalZ=1 AngleXU=0 Radius=1
    g40: Circle CenterX=-13.3521 CenterY=-17.9027 CenterZ=0 NormalX=0 NormalY=0 NormalZ=1 AngleXU=0 Radius=1
    g41: Circle CenterX=-14 CenterY=-18 CenterZ=0 NormalX=0 NormalY=0 NormalZ=1 AngleXU=0 Radius=1
    g42: BSplineCurve PolesCount=3 KnotsCount=2 Degree=2 IsPeriodic=0
    g43: GeomPoint X=-12.8401 Y=-17.6958 Z=0
    g44: GeomPoint X=-14 Y=-18 Z=0
    g45: LineSegment StartX=-6.2 StartY=0 StartZ=0 EndX=-7.2 EndY=0 EndZ=0
    g46: LineSegment StartX=-7.2 StartY=0 StartZ=0 EndX=-7.2 EndY=-2 EndZ=0
    g47: LineSegment StartX=-7.2 StartY=-2 StartZ=0 EndX=-6.2215 EndY=-2 EndZ=0
    g48: LineSegment StartX=-6.32538 StartY=-4 StartZ=0 EndX=-7.65538 EndY=-4 EndZ=0
    g49: LineSegment StartX=-7.65538 StartY=-4 StartZ=0 EndX=-7.65538 EndY=-5.99526 EndZ=0
    g50: LineSegment StartX=-7.65538 StartY=-5.99526 StartZ=0 EndX=-6.48644 EndY=-5.99526 EndZ=0
    g51: LineSegment StartX=-6.77343 StartY=-8 StartZ=0 EndX=-8.43343 EndY=-8 EndZ=0
    g52: LineSegment StartX=-8.43343 StartY=-8 StartZ=0 EndX=-8.43343 EndY=-10 EndZ=0
    g53: LineSegment StartX=-8.43343 StartY=-10 StartZ=0 EndX=-7.19003 EndY=-10 EndZ=0
  constraints (112):
    c: Horizontal(g0)
    c: Distance(g0) = 2
    c: Block(g0)
    c: Vertical(g1)
    c: Coincident(g2,g0)
    c: Vertical(g2)
    c: Block(g2)
    c: Coincident(g6,g2)
    c: Weight(g3) = 1
    c: Equal(g3,g4)
    c: Equal(g3,g5)
    c: InternalAlignment(g3,g6)
    c: InternalAlignment(g4,g6)
    c: InternalAlignment(g5,g6)
    c: InternalAlignment(g7,g6)
    c: InternalAlignment(g8,g6)
    c: Block(g6)
    c: Coincident(g9,g1)
    c: Coincident(g9,g6)
    c: Horizontal(g9)
    c: Vertical(g10)
    c: Block(g10)
    c: Horizontal(g11)
    c: Block(g11)
    c: Coincident(g12,g10)
    c: Horizontal(g12)
    c: Block(g12)
    c: Coincident(g13,g11)
    c: Vertical(g13)
    c: Block(g13)
    c: Coincident(g14,g10)
    c: Horizontal(g14)
    c: Block(g14)
    c: Block(g9)
    c: Block(g1)
    c: Weight(g15) = 1
    c: Equal(g15,g16)
    c: Equal(g15,g17)
    c: InternalAlignment(g15,g18)
    c: InternalAlignment(g16,g18)
    c: InternalAlignment(g17,g18)
    c: InternalAlignment(g19,g18)
    c: InternalAlignment(g20,g18)
    c: Weight(g21) = 1
    c: Equal(g21,g22)
    c: Equal(g21,g23)
    c: InternalAlignment(g21,g24)
    c: InternalAlignment(g22,g24)
    c: InternalAlignment(g23,g24)
    c: InternalAlignment(g25,g24)
    c: InternalAlignment(g26,g24)
    c: Weight(g27) = 1
    c: Equal(g27,g28)
    c: Equal(g27,g29)
    c: Coincident(g30,g14)
    c: InternalAlignment(g27,g30)
    c: InternalAlignment(g28,g30)
    c: InternalAlignment(g29,g30)
    c: InternalAlignment(g31,g30)
    c: InternalAlignment(g32,g30)
    c: Coincident(g36,g12)
    c: Weight(g33) = 1
    c: Equal(g33,g34)
    c: Equal(g33,g35)
    c: Coincident(g36,g11)
    c: InternalAlignment(g33,g36)
    c: InternalAlignment(g34,g36)
    c: InternalAlignment(g35,g36)
    c: InternalAlignment(g37,g36)
    c: InternalAlignment(g38,g36)
    c: Coincident(g42,g13)
    c: Weight(g39) = 1
    c: Equal(g39,g40)
    c: Equal(g39,g41)
    c: Coincident(g42,g1)
    c: InternalAlignment(g39,g42)
    c: InternalAlignment(g40,g42)
    c: InternalAlignment(g41,g42)
    c: InternalAlignment(g43,g42)
    c: InternalAlignment(g44,g42)
    c: Block(g18)
    c: Block(g24)
    c: Block(g30)
    c: Block(g36)
    c: Block(g42)
    c: Horizontal(g45)
    c: Coincident(g45,g0)
    c: Vertical(g46)
    c: Coincident(g46,g45)
    c: Coincident(g47,g46)
    c: Coincident(g47,g18)
    c: Horizontal(g47)
    c: Block(g46)
    c: Coincident(g48,g18)
    c: Horizontal(g48)
    c: Distance(g48) = 1.33
    c: Vertical(g49)
    c: Coincident(g49,g48)
    c: Coincident(g50,g49)
    c: Coincident(g50,g24)
    c: Horizontal(g50)
    c: Tangent(g50,g22)
    c: Horizontal(g51)
    c: Coincident(g51,g24)
    c: Block(g51)
    c: Vertical(g52)
    c: Block(g52)
    c: Coincident(g52,g51)
    c: Coincident(g53,g52)
    c: Coincident(g53,g30)
    c: Horizontal(g53)
    c: Distance(g1) = 8.5
FEATURE [Part::Feature] Face024
  shape: bbox 9.8 x 26.5 x 2e-07 mm, 1 faces, 0 solids (baked)
FEATURE [Part::Revolution] Revolve024
  Angle = 360
  Axis = (0,1,0)
  Base = (0,0,0)
  FaceMakerClass = Part::FaceMakerBullseye
  Placement = pos=(0,0,0) rot=(0,0,1;1.5708rad)
  Solid = false
  Source = -> Face024
  Symmetric = false
FEATURE [Part::Feature] Face025
  shape: bbox 9.8 x 26.5 x 2e-07 mm, 1 faces, 0 solids (baked)
FEATURE [Part::Revolution] Revolve025
  Angle = 360
  Axis = (0,1,0)
  Base = (0,0,0)
  FaceMakerClass = Part::FaceMakerBullseye
  Placement = pos=(0,0,0) rot=(0,0,1;1.5708rad)
  Solid = false
  Source = -> Face025
  Symmetric = false
FEATURE [Part::MultiFuse] Fusion033
  Placement = pos=(-18,19,36) rot=(0,0,1;0rad)
  Shapes = -> [Revolve025,Revolve024]
FEATURE [Part::Cylinder] Cylinder014
  Angle = 360
  AttacherType = Attacher::AttachEngine3D
  Height = 20
  Placement = pos=(0,0,36.15) rot=(0,0,1;0rad)
  Radius = 14.3
FEATURE [Part::Cylinder] Cylinder015
  Angle = 360
  AttacherType = Attacher::AttachEngine3D
  Height = 10
  Placement = pos=(0,0,36.15) rot=(0,0,1;0rad)
  Radius = 4
FEATURE [Part::MultiFuse] Fusion034  label="removeToCreteHoleForPlugHousing004"
  Placement = pos=(-42,19,36) rot=(0,1,0;1.5708rad)
  Shapes = -> [Cylinder014,Cylinder015]
FEATURE [Part::Cut] Cut008  label="top004"
  Base = -> Cut004
  Placement = pos=(-1,0,0) rot=(0,0,1;0rad)
  Tool = -> Fusion034
FEATURE [Part::Box] Box005  label="Cube005"
  AttacherType = Attacher::AttachEngine3D
  Height = 28
  Length = 3
  Placement = pos=(110.7,19,22) rot=(0,0,1;0rad)
  Width = 15.7
FEATURE [Part::Cylinder] Cylinder016
  Angle = 360
  AttacherType = Attacher::AttachEngine3D
  Height = 10
  Placement = pos=(0,0,36.15) rot=(0,0,1;0rad)
  Radius = 4
FEATURE [Part::Cylinder] Cylinder017
  Angle = 360
  AttacherType = Attacher::AttachEngine3D
  Height = 20
  Placement = pos=(0,0,36.15) rot=(0,0,1;0rad)
  Radius = 10.3
FEATURE [Part::MultiFuse] Fusion035  label="removeToCreteHoleForPlugHousing005"
  Placement = pos=(70,19,36) rot=(0,1,0;1.5708rad)
  Shapes = -> [Cylinder017,Cylinder016]
FEATURE [Part::Cut] Cut009  label="plugHousingTab001"
  Base = -> Box005
  Placement = pos=(-107.4,-14,0) rot=(0,0,1;0rad)
  Tool = -> Fusion035
FEATURE [Part::Box] Box006  label="Cube006"
  AttacherType = Attacher::AttachEngine3D
  Height = 28
  Length = 3
  Placement = pos=(110.7,19,22) rot=(0,0,1;0rad)
  Width = 15.7
FEATURE [Part::Cylinder] Cylinder018
  Angle = 360
  AttacherType = Attacher::AttachEngine3D
  Height = 10
  Placement = pos=(0,0,36.15) rot=(0,0,1;0rad)
  Radius = 4
FEATURE [Part::Cylinder] Cylinder019
  Angle = 360
  AttacherType = Attacher::AttachEngine3D
  Height = 20
  Placement = pos=(0,0,36.15) rot=(0,0,1;0rad)
  Radius = 10.3
FEATURE [Part::MultiFuse] Fusion036  label="removeToCreteHoleForPlugHousing006"
  Placement = pos=(70,19,36) rot=(0,1,0;1.5708rad)
  Shapes = -> [Cylinder019,Cylinder018]
FEATURE [Part::Cut] Cut010  label="plugHousingTab002"
  Base = -> Box006
  Placement = pos=(-107.4,-14,0) rot=(0,0,1;0rad)
  Tool = -> Fusion036
FEATURE [Part::MultiFuse] Fusion037
  Placement = pos=(9.6,23,0) rot=(0,0,1;3.14159rad)
  Shapes = -> [Cut009,Cut010]
FEATURE [Part::Box] Box  label="Cube"
  AttacherType = Attacher::AttachEngine3D
  Height = 10
  Length = 3
  Placement = pos=(3.3,4,12) rot=(0,0,1;0rad)
  Width = 10
FEATURE [Part::Fillet] Fillet004
  Base = -> Fusion028
  Edges = 1 edges r=2: [Edge25]
FEATURE [Part::Fillet] Fillet005  label="plugHousing046"
  Base = -> Fillet004
  Edges = 1 edges r=2: [Edge8]
FEATURE [Part::Fillet] Fillet006
  Base = -> Box
  Edges = 1 edges r=2: [Edge11]
FEATURE [Part::Box] Box007  label="Cube007"
  AttacherType = Attacher::AttachEngine3D
  Height = 10
  Length = 3
  Placement = pos=(3.3,4,50) rot=(0,0,1;0rad)
  Width = 10
FEATURE [Part::Fillet] Fillet007
  Base = -> Box007
  Edges = 1 edges r=2: [Edge12]
FEATURE [Part::Box] Box008  label="Cube008"
  AttacherType = Attacher::AttachEngine3D
  Height = 28
  Length = 4
  Placement = pos=(5,0,22) rot=(0,0,1;0rad)
  Width = 10
FEATURE [Part::Fillet] Fillet008
  Base = -> Box008
  Edges = 1 edges r=1: [Edge7]
FEATURE [Part::Fillet] Fillet009
  Base = -> Fillet008
  Edges = 1 edges r=2: [Edge5]
FEATURE [Part::Fillet] Fillet010
  Base = -> Fillet009
  Edges = 1 edges r=2: [Edge2]
FEATURE [Sketcher::SketchObject] Sketch009  label="topSketch003"
  FullyConstrained = true
  sketch-geometry (4):
    g0: LineSegment StartX=16.8446 StartY=31.512 StartZ=0 EndX=16.3251 EndY=34.4666 EndZ=0
    g1: ArcOfCircle CenterX=19 CenterY=19.2524 CenterZ=0 NormalX=0 NormalY=0 NormalZ=1 AngleXU=0 Radius=15.4476 StartAngle=1.74483 EndAngle=2.72717
    g2: ArcOfCircle CenterX=19 CenterY=19.2524 CenterZ=0 NormalX=0 NormalY=0 NormalZ=1 AngleXU=0 Radius=12.4476 StartAngle=1.74483 EndAngle=2.73189
    g3: LineSegment StartX=4.86004 StartY=25.4725 StartZ=0 EndX=7.58253 EndY=24.2107 EndZ=0
  constraints (7):
    c: Block(g0)
    c: Coincident(g1,g0)
    c: Coincident(g2,g0)
    c: Coincident(g3,g1)
    c: Coincident(g3,g2)
    c: Block(g1)
    c: Block(g2)
FEATURE [Part::Extrusion] Extrude008
  Base = -> Sketch009
  Dir = (0,0,1)
  DirMode = 2
  FaceMakerClass = Part::FaceMakerBullseye
  LengthFwd = 10
  LengthRev = 0
  Placement = pos=(0,0,31) rot=(0,0,1;0rad)
  Solid = true
  Symmetric = false
FEATURE [Part::Cylinder] Cylinder020
  Angle = 360
  AttacherType = Attacher::AttachEngine3D
  Height = 20
  Placement = pos=(0,0,36.15) rot=(0,0,1;0rad)
  Radius = 8.2
FEATURE [Part::Cylinder] Cylinder021
  Angle = 360
  AttacherType = Attacher::AttachEngine3D
  Height = 10
  Placement = pos=(0,0,36.15) rot=(0,0,1;0rad)
  Radius = 4
FEATURE [Part::MultiFuse] Fusion038  label="removeToCreteHoleForPlugHousing007"
  Placement = pos=(-42,19,36) rot=(0,1,0;1.5708rad)
  Shapes = -> [Cylinder020,Cylinder021]
FEATURE [Part::Cut] Cut011
  Base = -> Extrude008
  Tool = -> Fusion038
FEATURE [Part::Fillet] Fillet011
  Base = -> Cut011
  Edges = 1 edges r=2: [Edge1]
FEATURE [Part::Fillet] Fillet012
  Base = -> Fillet011
  Edges = 1 edges r=2.5: [Edge1]
FEATURE [Part::Fillet] Fillet013
  Base = -> Fillet012
  Edges = 1 edges r=2.5: [Edge2]
FEATURE [Part::Box] Box010  label="Cube010"
  AttacherType = Attacher::AttachEngine3D
  Height = 16
  Length = 8
  Placement = pos=(12.7,31.52,28) rot=(0,0,1;0rad)
  Width = 4
FEATURE [Sketcher::SketchObject] Sketch010  label="topSketch004"
  FullyConstrained = true
  sketch-geometry (4):
    g0: LineSegment StartX=16.8446 StartY=31.512 StartZ=0 EndX=16.3251 EndY=34.4666 EndZ=0
    g1: ArcOfCircle CenterX=19 CenterY=19.2524 CenterZ=0 NormalX=0 NormalY=0 NormalZ=1 AngleXU=0 Radius=15.4476 StartAngle=1.74483 EndAngle=2.72717
    g2: ArcOfCircle CenterX=19 CenterY=19.2524 CenterZ=0 NormalX=0 NormalY=0 NormalZ=1 AngleXU=0 Radius=12.4476 StartAngle=1.74483 EndAngle=2.73189
    g3: LineSegment StartX=4.86004 StartY=25.4725 StartZ=0 EndX=7.58253 EndY=24.2107 EndZ=0
  constraints (7):
    c: Block(g0)
    c: Coincident(g1,g0)
    c: Coincident(g2,g0)
    c: Coincident(g3,g1)
    c: Coincident(g3,g2)
    c: Block(g1)
    c: Block(g2)
FEATURE [Part::Cylinder] Cylinder022
  Angle = 360
  AttacherType = Attacher::AttachEngine3D
  Height = 10
  Placement = pos=(0,0,36.15) rot=(0,0,1;0rad)
  Radius = 4
FEATURE [Sketcher::SketchObject] Sketch011  label="topSketch005"
  FullyConstrained = true
  sketch-geometry (4):
    g0: LineSegment StartX=16.8446 StartY=31.512 StartZ=0 EndX=16.3251 EndY=34.4666 EndZ=0
    g1: ArcOfCircle CenterX=19 CenterY=19.2524 CenterZ=0 NormalX=0 NormalY=0 NormalZ=1 AngleXU=0 Radius=15.4476 StartAngle=1.74483 EndAngle=2.72717
    g2: ArcOfCircle CenterX=19 CenterY=19.2524 CenterZ=0 NormalX=0 NormalY=0 NormalZ=1 AngleXU=0 Radius=12.4476 StartAngle=1.74483 EndAngle=2.73189
    g3: LineSegment StartX=4.86004 StartY=25.4725 StartZ=0 EndX=7.58253 EndY=24.2107 EndZ=0
  constraints (7):
    c: Block(g0)
    c: Coincident(g1,g0)
    c: Coincident(g2,g0)
    c: Coincident(g3,g1)
    c: Coincident(g3,g2)
    c: Block(g1)
    c: Block(g2)
FEATURE [Part::Extrusion] Extrude010
  Base = -> Sketch011
  Dir = (0,0,1)
  DirMode = 2
  FaceMakerClass = Part::FaceMakerBullseye
  LengthFwd = 10.6
  LengthRev = 0
  Placement = pos=(0,0,31) rot=(0,0,1;0rad)
  Solid = true
  Symmetric = false
FEATURE [Part::Cylinder] Cylinder023
  Angle = 360
  AttacherType = Attacher::AttachEngine3D
  Height = 20
  Placement = pos=(0,0,36.15) rot=(0,0,1;0rad)
  Radius = 8.2
FEATURE [Part::MultiFuse] Fusion039  label="removeToCreteHoleForPlugHousing008"
  Placement = pos=(-42,19,36) rot=(0,1,0;1.5708rad)
  Shapes = -> [Cylinder023,Cylinder022]
FEATURE [Part::Cut] Cut012
  Base = -> Extrude010
  Placement = pos=(0,0,-0.3) rot=(0,0,1;0rad)
  Tool = -> Fusion039
FEATURE [Part::Cut] Cut013
  Base = -> Box010
  Tool = -> Cut012
FEATURE [Part::Fillet] Fillet014
  Base = -> Cut013
  Edges = 1 edges r=0.7: [Edge13]
FEATURE [Part::Fillet] Fillet015
  Base = -> Fillet014
  Edges = 1 edges r=0.7: [Edge13]
FEATURE [Part::Fillet] Fillet016
  Base = -> Fillet015
  Edges = 1 edges r=0.7: [Edge16]
FEATURE [Part::Fillet] Fillet017
  Base = -> Fillet016
  Edges = 1 edges r=0.7: [Edge11]
FEATURE [Part::Fillet] Fillet018
  Base = -> Fillet017
  Edges = 1 edges r=0.7: [Edge10]
FEATURE [Part::Fillet] Fillet019
  Base = -> Fillet018
  Edges = 1 edges r=1.2: [Edge5]
FEATURE [Part::Fillet] Fillet020
  Base = -> Fillet019
  Edges = 1 edges r=1.2: [Edge12]
FEATURE [Part::Fillet] Fillet021
  Base = -> Fillet020
  Edges = 1 edges r=2: [Edge1]
  Placement = pos=(0.3,0,0) rot=(0,0,1;0rad)
FEATURE [Part::MultiFuse] Fusion040  label="top005"
  Shapes = -> [Cut008,Fillet021]
FEATURE [Part::MultiFuse] Fusion041  label="wireHolder"
  Shapes = -> [Fusion033,Fillet013]
FEATURE [Part::MultiFuse] Fusion042
  Shapes = -> [Fillet007,Fusion041]
FEATURE [Part::MultiFuse] Fusion043  label="wireHolder001"
  Shapes = -> [Fusion042,Fillet010]
FEATURE [Part::MultiFuse] Fusion044  label="wireHolder002"
  Shapes = -> [Fillet006,Fusion037,Fusion043]
FEATURE [Part::Feature] Face026
  shape: bbox 11 x 6 x 2e-07 mm, 1 faces, 0 solids (baked)
FEATURE [Part::Revolution] Revolve026
  Angle = 360
  Axis = (0,1,0)
  Base = (0,0,0)
  FaceMakerClass = Part::FaceMakerBullseye
  Placement = pos=(30.3,-1,19.7) rot=(0,0,1;0rad)
  Solid = false
  Source = -> Face026
  Symmetric = false
FEATURE [Sketcher::SketchObject] Sketch013  label="topSketch006"
  FullyConstrained = true
  sketch-geometry (13):
    g0: LineSegment StartX=117 StartY=19 StartZ=0 EndX=117 EndY=38 EndZ=0
    g1: ArcOfCircle CenterX=98 CenterY=19 CenterZ=0 NormalX=0 NormalY=0 NormalZ=1 AngleXU=0 Radius=19 StartAngle=5.7297 EndAngle=6.28319
    g2: LineSegment StartX=0 StartY=3 StartZ=0 EndX=0 EndY=19 EndZ=0
    g3: LineSegment StartX=19 StartY=38 StartZ=0 EndX=117 EndY=38 EndZ=0
    g4: ArcOfCircle CenterX=19 CenterY=19 CenterZ=0 NormalX=0 NormalY=0 NormalZ=1 AngleXU=0 Radius=19 StartAngle=1.5708 EndAngle=3.14159
    g5: ArcOfCircle CenterX=19 CenterY=19 CenterZ=0 NormalX=0 NormalY=0 NormalZ=1 AngleXU=0 Radius=16 StartAngle=1.5708 EndAngle=3.14159
    g6: ArcOfCircle CenterX=98 CenterY=19 CenterZ=0 NormalX=0 NormalY=0 NormalZ=1 AngleXU=0 Radius=16 StartAngle=5.60905 EndAngle=6.28319
    g7: LineSegment StartX=114 StartY=19 StartZ=0 EndX=114 EndY=35 EndZ=0
    g8: LineSegment StartX=110.5 StartY=9.01251 StartZ=0 EndX=114.163 EndY=9.01251 EndZ=0
    g9: LineSegment StartX=114 StartY=35 StartZ=0 EndX=19 EndY=35 EndZ=0
    g10: LineSegment StartX=0 StartY=3 StartZ=0 EndX=0 EndY=0 EndZ=0
    g11: LineSegment StartX=3 StartY=0 StartZ=0 EndX=0 EndY=0 EndZ=0
    g12: LineSegment StartX=3 StartY=19 StartZ=0 EndX=3 EndY=0 EndZ=0
  constraints (33):
    c: Vertical(g0)
    c: Distance(g0) = 19
    c: Block(g0)
    c: Coincident(g1,g0)
    c: Block(g1)
    c: Vertical(g2)
    c: Block(g2)
    c: Coincident(g3,g0)
    c: Horizontal(g3)
    c: Distance(g3) = 98
    c: Coincident(g4,g3)
    c: Coincident(g4,g2)
    c: Block(g4)
    c: Coincident(g5,g4)
    c: Coincident(g6,g1)
    c: Block(g6)
    c: Block(g5)
    c: Coincident(g7,g6)
    c: Vertical(g7)
    c: Coincident(g8,g6)
    c: Coincident(g8,g1)
    c: Coincident(g9,g7)
    c: Coincident(g9,g5)
    c: Horizontal(g9)
    c: Tangent(g9,g5)
    c: Coincident(g10,g2)
    c: Distance(g10) = 3
    c: Vertical(g10)
    c: Coincident(g11,g10)
    c: Horizontal(g11)
    c: Coincident(g12,g5)
    c: Coincident(g12,g11)
    c: Vertical(g12)
FEATURE [Part::Extrusion] Extrude011  label="top006"
  Base = -> Sketch013
  Dir = (0,0,1)
  DirMode = 2
  FaceMakerClass = Part::FaceMakerBullseye
  LengthFwd = 72
  LengthRev = 0
  Solid = true
  Symmetric = false
FEATURE [Sketcher::SketchObject] Sketch014
  FullyConstrained = true
  MapMode = 3
  Placement = pos=(0,0,0) rot=(1,0,0;1.5708rad)
  Support = -> [Extrude011]
  sketch-geometry (8):
    g0: Circle CenterX=80.351 CenterY=-67.6202 CenterZ=0 NormalX=0 NormalY=0 NormalZ=1 AngleXU=0 Radius=2
    g1: Circle CenterX=80.351 CenterY=-67.6202 CenterZ=0 NormalX=0 NormalY=0 NormalZ=1 AngleXU=0 Radius=3
    g2: Circle CenterX=80.351 CenterY=-4.92017 CenterZ=0 NormalX=0 NormalY=0 NormalZ=1 AngleXU=0 Radius=2
    g3: Circle CenterX=80.351 CenterY=-4.92017 CenterZ=0 NormalX=0 NormalY=0 NormalZ=1 AngleXU=0 Radius=3
    g4: Circle CenterX=23.851 CenterY=-4.92017 CenterZ=0 NormalX=0 NormalY=0 NormalZ=1 AngleXU=0 Radius=2
    g5: Circle CenterX=23.851 CenterY=-4.92017 CenterZ=0 NormalX=0 NormalY=0 NormalZ=1 AngleXU=0 Radius=3
    g6: Circle CenterX=23.851 CenterY=-67.6202 CenterZ=0 NormalX=0 NormalY=0 NormalZ=1 AngleXU=0 Radius=2
    g7: Circle CenterX=23.851 CenterY=-67.6202 CenterZ=0 NormalX=0 NormalY=0 NormalZ=1 AngleXU=0 Radius=3
  constraints (8):
    c: Block(g3)
    c: Block(g2)
    c: Block(g1)
    c: Block(g0)
    c: Block(g6)
    c: Block(g7)
    c: Block(g4)
    c: Block(g5)
FEATURE [Part::Feature] Face027
  shape: bbox 11 x 6 x 2e-07 mm, 1 faces, 0 solids (baked)
FEATURE [Part::Revolution] Revolve027
  Angle = 360
  Axis = (0,1,0)
  Base = (0,0,0)
  FaceMakerClass = Part::FaceMakerBullseye
  Placement = pos=(30.3,-1,51.7) rot=(0,0,1;0rad)
  Solid = false
  Source = -> Face027
  Symmetric = false
FEATURE [Part::Feature] Face028
  shape: bbox 11 x 6 x 2e-07 mm, 1 faces, 0 solids (baked)
FEATURE [Part::Revolution] Revolve028
  Angle = 360
  Axis = (0,1,0)
  Base = (0,0,0)
  FaceMakerClass = Part::FaceMakerBullseye
  Placement = pos=(62.3,-1,19.7) rot=(0,0,1;0rad)
  Solid = false
  Source = -> Face028
  Symmetric = false
FEATURE [Part::Feature] Face029
  shape: bbox 11 x 6 x 2e-07 mm, 1 faces, 0 solids (baked)
FEATURE [Part::Revolution] Revolve029
  Angle = 360
  Axis = (0,1,0)
  Base = (0,0,0)
  FaceMakerClass = Part::FaceMakerBullseye
  Placement = pos=(62.3,-1,51.7) rot=(0,0,1;0rad)
  Solid = false
  Source = -> Face029
  Symmetric = false
FEATURE [Part::Feature] Wire
  shape: bbox 11 x 5.2 x 2e-07 mm, 0 faces, 0 solids (baked)
FEATURE [Part::Revolution] Revolve030
  Angle = 360
  Axis = (0,1,0)
  Base = (0,0,0)
  FaceMakerClass = Part::FaceMakerBullseye
  Placement = pos=(30.3,38,19.7) rot=(0,0,1;0rad)
  Solid = true
  Source = -> Wire
  Symmetric = false
FEATURE [Part::Feature] Wire001
  shape: bbox 11 x 5.2 x 2e-07 mm, 0 faces, 0 solids (baked)
FEATURE [Part::Revolution] Revolve031
  Angle = 360
  Axis = (0,1,0)
  Base = (0,0,0)
  FaceMakerClass = Part::FaceMakerBullseye
  Placement = pos=(30.3,38,51.7) rot=(0,0,1;0rad)
  Solid = true
  Source = -> Wire001
  Symmetric = false
FEATURE [Part::Feature] Wire002
  shape: bbox 11 x 5.2 x 2e-07 mm, 0 faces, 0 solids (baked)
FEATURE [Part::Revolution] Revolve032
  Angle = 360
  Axis = (0,1,0)
  Base = (0,0,0)
  FaceMakerClass = Part::FaceMakerBullseye
  Placement = pos=(62.3,38,51.7) rot=(0,0,1;0rad)
  Solid = true
  Source = -> Wire002
  Symmetric = false
FEATURE [Part::Feature] Wire003
  shape: bbox 11 x 5.2 x 2e-07 mm, 0 faces, 0 solids (baked)
FEATURE [Part::Revolution] Revolve033
  Angle = 360
  Axis = (0,1,0)
  Base = (0,0,0)
  FaceMakerClass = Part::FaceMakerBullseye
  Placement = pos=(62.3,38,19.7) rot=(0,0,1;0rad)
  Solid = true
  Source = -> Wire003
  Symmetric = false
FEATURE [Part::MultiFuse] Fusion045  label="altRandScrewHousing"
  Shapes = -> [Revolve029,Revolve027,Revolve028,Revolve026]
FEATURE [Part::MultiFuse] Fusion046  label="fanScrewHousing"
  Shapes = -> [Revolve033,Revolve032,Revolve031,Revolve030]
FEATURE [Sketcher::SketchObject] Sketch015
  FullyConstrained = true
  sketch-geometry (17):
    g0: Circle CenterX=-3.5 CenterY=23.5 CenterZ=0 NormalX=0 NormalY=0 NormalZ=1 AngleXU=0 Radius=1
    g1: Circle CenterX=-1 CenterY=15.25 CenterZ=0 NormalX=0 NormalY=0 NormalZ=1 AngleXU=0 Radius=1
    g2: Circle CenterX=-3.5 CenterY=7 CenterZ=0 NormalX=0 NormalY=0 NormalZ=1 AngleXU=0 Radius=1
    g3: BSplineCurve PolesCount=3 KnotsCount=2 Degree=2 IsPeriodic=0
    g4: GeomPoint X=-3.5 Y=23.5 Z=0
    g5: GeomPoint X=-3.5 Y=7 Z=0
    g6: Circle CenterX=-4.8 CenterY=30.5 CenterZ=0 NormalX=0 NormalY=0 NormalZ=1 AngleXU=0 Radius=1
    g7: Circle CenterX=-3.5 CenterY=30.5 CenterZ=0 NormalX=0 NormalY=0 NormalZ=1 AngleXU=0 Radius=1
    g8: Circle CenterX=-3.5 CenterY=29.2 CenterZ=0 NormalX=0 NormalY=0 NormalZ=1 AngleXU=0 Radius=1
    g9: BSplineCurve PolesCount=3 KnotsCount=2 Degree=2 IsPeriodic=0
    g10: GeomPoint X=-4.8 Y=30.5 Z=0
    g11: GeomPoint X=-3.5 Y=29.2 Z=0
    g12: LineSegment StartX=-3.5 StartY=29.2 StartZ=0 EndX=-3.5 EndY=23.5 EndZ=0
    g13: LineSegment StartX=-4.8 StartY=30.5 StartZ=0 EndX=0 EndY=30.5 EndZ=0
    g14: LineSegment StartX=-3.5 StartY=0.3 StartZ=0 EndX=0 EndY=0.3 EndZ=0
    g15: LineSegment StartX=-3.5 StartY=0.3 StartZ=0 EndX=-3.5 EndY=7 EndZ=0
    g16: LineSegment StartX=0 StartY=0.3 StartZ=0 EndX=0 EndY=30.5 EndZ=0
  constraints (33):
    c: Weight(g0) = 1
    c: Equal(g0,g1)
    c: Equal(g0,g2)
    c: InternalAlignment(g0,g3)
    c: InternalAlignment(g1,g3)
    c: InternalAlignment(g2,g3)
    c: InternalAlignment(g4,g3)
    c: InternalAlignment(g5,g3)
    c: Block(g3)
    c: Weight(g6) = 1
    c: Equal(g6,g7)
    c: Equal(g6,g8)
    c: InternalAlignment(g6,g9)
    c: InternalAlignment(g7,g9)
    c: InternalAlignment(g8,g9)
    c: InternalAlignment(g10,g9)
    c: InternalAlignment(g11,g9)
    c: Block(g9)
    c: Coincident(g12,g9)
    c: Coincident(g12,g3)
    c: Vertical(g12)
    c: Coincident(g13,g9)
    c: Horizontal(g13)
    c: Distance(g13) = 4.8
    c: Horizontal(g14)
    c: Block(g14)
    c: Coincident(g15,g14)
    c: Coincident(g15,g3)
    c: Vertical(g15)
    c: Coincident(g16,g14)
    c: Coincident(g16,g13)
    c: Vertical(g16)
    c: Tangent(g16,g1)
FEATURE [Sketcher::SketchObject] Sketch016
  FullyConstrained = true
  sketch-geometry (16):
    g0: Circle CenterX=-3.5 CenterY=23.5 CenterZ=0 NormalX=0 NormalY=0 NormalZ=1 AngleXU=0 Radius=1
    g1: Circle CenterX=-1 CenterY=15.25 CenterZ=0 NormalX=0 NormalY=0 NormalZ=1 AngleXU=0 Radius=1
    g2: Circle CenterX=-3.5 CenterY=7 CenterZ=0 NormalX=0 NormalY=0 NormalZ=1 AngleXU=0 Radius=1
    g3: BSplineCurve PolesCount=3 KnotsCount=2 Degree=2 IsPeriodic=0
    g4: GeomPoint X=-3.5 Y=23.5 Z=0
    g5: GeomPoint X=-3.5 Y=7 Z=0
    g6: LineSegment StartX=-3.5 StartY=28.2 StartZ=0 EndX=-3.5 EndY=23.5 EndZ=0
    g7: LineSegment StartX=0 StartY=29.5 StartZ=0 EndX=0 EndY=30 EndZ=0
    g8: LineSegment StartX=-3.5 StartY=28.2 StartZ=0 EndX=-3.5 EndY=30 EndZ=0
    g9: LineSegment StartX=0 StartY=30 StartZ=0 EndX=0 EndY=30.5 EndZ=0
    g10: LineSegment StartX=0 StartY=30.5 StartZ=0 EndX=-3.5 EndY=30.5 EndZ=0
    g11: LineSegment StartX=-3.5 StartY=30.5 StartZ=0 EndX=-3.5 EndY=30 EndZ=0
    g12: LineSegment StartX=0 StartY=29.5 StartZ=0 EndX=0 EndY=5 EndZ=0
    g13: LineSegment StartX=-3.5 StartY=0.3 StartZ=0 EndX=-3.5 EndY=7 EndZ=0
    g14: LineSegment StartX=-3.5 StartY=0.3 StartZ=0 EndX=0 EndY=0.3 EndZ=0
    g15: LineSegment StartX=0 StartY=5 StartZ=0 EndX=0 EndY=0.3 EndZ=0
  constraints (39):
    c: Weight(g0) = 1
    c: Equal(g0,g1)
    c: Equal(g0,g2)
    c: InternalAlignment(g0,g3)
    c: InternalAlignment(g1,g3)
    c: InternalAlignment(g2,g3)
    c: InternalAlignment(g4,g3)
    c: InternalAlignment(g5,g3)
    c: Block(g3)
    c: Coincident(g6,g3)
    c: Vertical(g6)
    c: Vertical(g7)
    c: Distance(g7) = 0.5
    c: Coincident(g8,g6)
    c: Vertical(g8)
    c: Block(g6)
    c: Block(g7)
    c: Vertical(g9)
    c: Equal(g7,g9) = 0.5
    c: Block(g9)
    c: Coincident(g9,g7)
    c: Horizontal(g10)
    c: Coincident(g10,g9)
    c: Coincident(g11,g10)
    c: Coincident(g11,g8)
    c: Vertical(g11)
    c: Block(g11)
    c: Coincident(g12,g7)
    c: Vertical(g12)
    c: Coincident(g13,g3)
    c: Vertical(g13)
    c: Distance(g13) = 6.7
    c: Coincident(g14,g13)
    c: Horizontal(g14)
    c: Block(g14)
    c: Coincident(g15,g12)
    c: Coincident(g15,g14)
    c: Vertical(g15)
    c: Block(g15)
FEATURE [Sketcher::SketchObject] Sketch017
  FullyConstrained = true
  sketch-geometry (11):
    g0: LineSegment StartX=-3.5 StartY=1e-16 StartZ=0 EndX=-1.6 EndY=1e-16 EndZ=0
    g1: LineSegment StartX=-1.6 StartY=1e-16 StartZ=0 EndX=-1.6 EndY=1.5 EndZ=0
    g2: LineSegment StartX=-3.5 StartY=1.5 StartZ=0 EndX=-1.6 EndY=1.5 EndZ=0
    g3: LineSegment StartX=-3.5 StartY=1e-16 StartZ=0 EndX=-4.8 EndY=1e-16 EndZ=0
    g4: Circle CenterX=-3.5 CenterY=1.3 CenterZ=0 NormalX=0 NormalY=0 NormalZ=1 AngleXU=0 Radius=1
    g5: Circle CenterX=-3.5 CenterY=1e-16 CenterZ=0 NormalX=0 NormalY=0 NormalZ=1 AngleXU=0 Radius=1
    g6: Circle CenterX=-4.8 CenterY=1e-16 CenterZ=0 NormalX=0 NormalY=0 NormalZ=1 AngleXU=0 Radius=1
    g7: BSplineCurve PolesCount=3 KnotsCount=2 Degree=2 IsPeriodic=0
    g8: GeomPoint X=-3.5 Y=1.3 Z=0
    g9: GeomPoint X=-4.8 Y=1e-16 Z=0
    g10: LineSegment StartX=-3.5 StartY=1.3 StartZ=0 EndX=-3.5 EndY=1.5 EndZ=0
  constraints (24):
    c: Horizontal(g0)
    c: Distance(g0) = 1.9
    c: Block(g0)
    c: Coincident(g1,g0)
    c: Vertical(g1)
    c: Coincident(g2,g1)
    c: Horizontal(g2)
    c: Coincident(g3,g0)
    c: Horizontal(g3)
    c: Distance(g3) = 1.3
    c: Weight(g4) = 1
    c: Equal(g4,g5)
    c: Coincident(g5,g0)
    c: Equal(g4,g6)
    c: Coincident(g7,g3)
    c: InternalAlignment(g4,g7)
    c: InternalAlignment(g5,g7)
    c: InternalAlignment(g6,g7)
    c: InternalAlignment(g8,g7)
    c: InternalAlignment(g9,g7)
    c: Coincident(g10,g7)
    c: Coincident(g10,g2)
    c: Vertical(g10)
    c: Block(g10)
FEATURE [Part::Feature] Face035
  shape: bbox 3.2 x 1.5 x 2e-07 mm, 1 faces, 0 solids (baked)
FEATURE [Part::Revolution] Revolve039  label="backCaseScrewRetainer"
  Angle = 360
  Axis = (0,1,0)
  Base = (0,0,0)
  FaceMakerClass = Part::FaceMakerBullseye
  Placement = pos=(12.5,3,62) rot=(0,0,1;0rad)
  Solid = false
  Source = -> Face035
  Symmetric = false
FEATURE [Part::Feature] Face036
  shape: bbox 3.2 x 1.5 x 2e-07 mm, 1 faces, 0 solids (baked)
FEATURE [Part::Feature] Face039
  shape: bbox 4.8 x 30.2 x 2e-07 mm, 1 faces, 0 solids (baked)
FEATURE [Part::Revolution] Revolve043  label="frontCaseScrewPost002"
  Angle = 360
  Axis = (0,1,0)
  Base = (0,0,0)
  FaceMakerClass = Part::FaceMakerBullseye
  Placement = pos=(89.5,4.5,3.5) rot=(0,0,1;0rad)
  Solid = false
  Source = -> Face039
  Symmetric = false
FEATURE [Part::Feature] Face042
  shape: bbox 4.8 x 30.2 x 2e-07 mm, 1 faces, 0 solids (baked)
FEATURE [Part::Revolution] Revolve046  label="frontCaseScrewPost003"
  Angle = 360
  Axis = (0,1,0)
  Base = (0,0,0)
  FaceMakerClass = Part::FaceMakerBullseye
  Placement = pos=(89.5,4.5,68.5) rot=(0,0,1;0rad)
  Solid = false
  Source = -> Face042
  Symmetric = false
FEATURE [Part::Feature] Face043
  shape: bbox 3.2 x 1.5 x 2e-07 mm, 1 faces, 0 solids (baked)
FEATURE [Part::Revolution] Revolve047  label="frontCaseScrewRetainer002"
  Angle = 360
  Axis = (0,1,0)
  Base = (0,0,0)
  FaceMakerClass = Part::FaceMakerBullseye
  Placement = pos=(89.5,3,68.5) rot=(0,0,1;0rad)
  Solid = false
  Source = -> Face043
  Symmetric = false
FEATURE [Part::Feature] Face044
  shape: bbox 3.2 x 1.5 x 2e-07 mm, 1 faces, 0 solids (baked)
FEATURE [Part::Revolution] Revolve048  label="frontCaseScrewRetainer003"
  Angle = 360
  Axis = (0,1,0)
  Base = (0,0,0)
  FaceMakerClass = Part::FaceMakerBullseye
  Placement = pos=(89.5,3,3.5) rot=(0,0,1;0rad)
  Solid = false
  Source = -> Face044
  Symmetric = false
FEATURE [App::MeasureDistance] Distance002  label="Distance: 1.67 mm"
  Distance = 1.66921
  P1 = (99.2361,4.7524,71.7)
  P2 = (99.2347,6.42161,71.7)
FEATURE [Sketcher::SketchObject] Sketch018
  FullyConstrained = true
  sketch-geometry (7):
    g0: LineSegment StartX=0 StartY=0 StartZ=0 EndX=0 EndY=6 EndZ=0
    g1: Circle CenterX=0 CenterY=0 CenterZ=0 NormalX=0 NormalY=0 NormalZ=1 AngleXU=0 Radius=1
    g2: Circle CenterX=8 CenterY=6 CenterZ=0 NormalX=0 NormalY=0 NormalZ=1 AngleXU=0 Radius=1
    g3: BSplineCurve PolesCount=3 KnotsCount=2 Degree=2 IsPeriodic=0
    g4: GeomPoint X=0 Y=0 Z=0
    g5: GeomPoint X=8 Y=6 Z=0
    g6: LineSegment StartX=0 StartY=6 StartZ=0 EndX=8 EndY=6 EndZ=0
  constraints (14):
    c: Coincident(g0,g-1)
    c: Distance(g0) = 6
    c: Vertical(g0)
    c: Coincident(g3,g0)
    c: Weight(g1) = 1
    c: Equal(g1,g2)
    c: InternalAlignment(g1,g3)
    c: InternalAlignment(g2,g3)
    c: InternalAlignment(g4,g3)
    c: InternalAlignment(g5,g3)
    c: Block(g3)
    c: Coincident(g6,g0)
    c: Coincident(g6,g3)
    c: Horizontal(g6)
FEATURE [Part::Extrusion] Extrude012  label="caseScrewPillarBracket"
  Base = -> Sketch018
  Dir = (0,0,1)
  DirMode = 2
  FaceMakerClass = Part::FaceMakerBullseye
  LengthFwd = 2.4
  LengthRev = 0
  Placement = pos=(15.76,29,8.8) rot=(0,1,0;0rad)
  Solid = true
  Symmetric = false
FEATURE [Sketcher::SketchObject] Sketch019
  FullyConstrained = true
  sketch-geometry (7):
    g0: LineSegment StartX=0 StartY=0 StartZ=0 EndX=0 EndY=6 EndZ=0
    g1: Circle CenterX=0 CenterY=0 CenterZ=0 NormalX=0 NormalY=0 NormalZ=1 AngleXU=0 Radius=1
    g2: Circle CenterX=8 CenterY=6 CenterZ=0 NormalX=0 NormalY=0 NormalZ=1 AngleXU=0 Radius=1
    g3: BSplineCurve PolesCount=3 KnotsCount=2 Degree=2 IsPeriodic=0
    g4: GeomPoint X=0 Y=0 Z=0
    g5: GeomPoint X=8 Y=6 Z=0
    g6: LineSegment StartX=0 StartY=6 StartZ=0 EndX=8 EndY=6 EndZ=0
  constraints (14):
    c: Coincident(g0,g-1)
    c: Distance(g0) = 6
    c: Vertical(g0)
    c: Coincident(g3,g0)
    c: Weight(g1) = 1
    c: Equal(g1,g2)
    c: InternalAlignment(g1,g3)
    c: InternalAlignment(g2,g3)
    c: InternalAlignment(g4,g3)
    c: InternalAlignment(g5,g3)
    c: Block(g3)
    c: Coincident(g6,g0)
    c: Coincident(g6,g3)
    c: Horizontal(g6)
FEATURE [Part::Extrusion] Extrude013  label="caseScrewPillarBracket001"
  Base = -> Sketch019
  Dir = (0,0,1)
  DirMode = 2
  FaceMakerClass = Part::FaceMakerBullseye
  LengthFwd = 2.4
  LengthRev = 0
  Placement = pos=(15.76,29,60.8) rot=(0,0,1;0rad)
  Solid = true
  Symmetric = false
FEATURE [Sketcher::SketchObject] Sketch020
  FullyConstrained = true
  sketch-geometry (7):
    g0: LineSegment StartX=0 StartY=0 StartZ=0 EndX=0 EndY=6 EndZ=0
    g1: Circle CenterX=0 CenterY=0 CenterZ=0 NormalX=0 NormalY=0 NormalZ=1 AngleXU=0 Radius=1
    g2: Circle CenterX=8 CenterY=6 CenterZ=0 NormalX=0 NormalY=0 NormalZ=1 AngleXU=0 Radius=1
    g3: BSplineCurve PolesCount=3 KnotsCount=2 Degree=2 IsPeriodic=0
    g4: GeomPoint X=0 Y=0 Z=0
    g5: GeomPoint X=8 Y=6 Z=0
    g6: LineSegment StartX=0 StartY=6 StartZ=0 EndX=8 EndY=6 EndZ=0
  constraints (14):
    c: Coincident(g0,g-1)
    c: Distance(g0) = 6
    c: Vertical(g0)
    c: Coincident(g3,g0)
    c: Weight(g1) = 1
    c: Equal(g1,g2)
    c: InternalAlignment(g1,g3)
    c: InternalAlignment(g2,g3)
    c: InternalAlignment(g4,g3)
    c: InternalAlignment(g5,g3)
    c: Block(g3)
    c: Coincident(g6,g0)
    c: Coincident(g6,g3)
    c: Horizontal(g6)
FEATURE [Part::Extrusion] Extrude014  label="caseScrewPillarBracket002"
  Base = -> Sketch020
  Dir = (0,0,1)
  DirMode = 2
  FaceMakerClass = Part::FaceMakerBullseye
  LengthFwd = 2.4
  LengthRev = 0
  Placement = pos=(13.7,29,13.26) rot=(0,-1,0;1.5708rad)
  Solid = true
  Symmetric = false
FEATURE [Sketcher::SketchObject] Sketch021
  FullyConstrained = true
  sketch-geometry (7):
    g0: LineSegment StartX=0 StartY=0 StartZ=0 EndX=0 EndY=6 EndZ=0
    g1: Circle CenterX=0 CenterY=0 CenterZ=0 NormalX=0 NormalY=0 NormalZ=1 AngleXU=0 Radius=1
    g2: Circle CenterX=8 CenterY=6 CenterZ=0 NormalX=0 NormalY=0 NormalZ=1 AngleXU=0 Radius=1
    g3: BSplineCurve PolesCount=3 KnotsCount=2 Degree=2 IsPeriodic=0
    g4: GeomPoint X=0 Y=0 Z=0
    g5: GeomPoint X=8 Y=6 Z=0
    g6: LineSegment StartX=0 StartY=6 StartZ=0 EndX=8 EndY=6 EndZ=0
  constraints (14):
    c: Coincident(g0,g-1)
    c: Distance(g0) = 6
    c: Vertical(g0)
    c: Coincident(g3,g0)
    c: Weight(g1) = 1
    c: Equal(g1,g2)
    c: InternalAlignment(g1,g3)
    c: InternalAlignment(g2,g3)
    c: InternalAlignment(g4,g3)
    c: InternalAlignment(g5,g3)
    c: Block(g3)
    c: Coincident(g6,g0)
    c: Coincident(g6,g3)
    c: Horizontal(g6)
FEATURE [Part::Extrusion] Extrude015  label="caseScrewPillarBracket003"
  Base = -> Sketch021
  Dir = (0,0,1)
  DirMode = 2
  FaceMakerClass = Part::FaceMakerBullseye
  LengthFwd = 2.4
  LengthRev = 0
  Placement = pos=(11.3,29,58.74) rot=(0,1,0;1.5708rad)
  Solid = true
  Symmetric = false
FEATURE [Sketcher::SketchObject] Sketch022
  FullyConstrained = true
  sketch-geometry (7):
    g0: LineSegment StartX=0 StartY=0 StartZ=0 EndX=0 EndY=6 EndZ=0
    g1: Circle CenterX=0 CenterY=0 CenterZ=0 NormalX=0 NormalY=0 NormalZ=1 AngleXU=0 Radius=1
    g2: Circle CenterX=8 CenterY=6 CenterZ=0 NormalX=0 NormalY=0 NormalZ=1 AngleXU=0 Radius=1
    g3: BSplineCurve PolesCount=3 KnotsCount=2 Degree=2 IsPeriodic=0
    g4: GeomPoint X=0 Y=0 Z=0
    g5: GeomPoint X=8 Y=6 Z=0
    g6: LineSegment StartX=0 StartY=6 StartZ=0 EndX=8 EndY=6 EndZ=0
  constraints (14):
    c: Coincident(g0,g-1)
    c: Distance(g0) = 6
    c: Vertical(g0)
    c: Coincident(g3,g0)
    c: Weight(g1) = 1
    c: Equal(g1,g2)
    c: InternalAlignment(g1,g3)
    c: InternalAlignment(g2,g3)
    c: InternalAlignment(g4,g3)
    c: InternalAlignment(g5,g3)
    c: Block(g3)
    c: Coincident(g6,g0)
    c: Coincident(g6,g3)
    c: Horizontal(g6)
FEATURE [Part::Extrusion] Extrude016  label="caseScrewPillarBracket004"
  Base = -> Sketch022
  Dir = (0,0,1)
  DirMode = 2
  FaceMakerClass = Part::FaceMakerBullseye
  LengthFwd = 2.4
  LengthRev = 0
  Placement = pos=(88.3,29,65.23) rot=(0,1,0;1.5708rad)
  Solid = true
  Symmetric = false
FEATURE [Sketcher::SketchObject] Sketch023
  FullyConstrained = true
  sketch-geometry (7):
    g0: LineSegment StartX=0 StartY=0 StartZ=0 EndX=0 EndY=6 EndZ=0
    g1: Circle CenterX=0 CenterY=0 CenterZ=0 NormalX=0 NormalY=0 NormalZ=1 AngleXU=0 Radius=1
    g2: Circle CenterX=8 CenterY=6 CenterZ=0 NormalX=0 NormalY=0 NormalZ=1 AngleXU=0 Radius=1
    g3: BSplineCurve PolesCount=3 KnotsCount=2 Degree=2 IsPeriodic=0
    g4: GeomPoint X=0 Y=0 Z=0
    g5: GeomPoint X=8 Y=6 Z=0
    g6: LineSegment StartX=0 StartY=6 StartZ=0 EndX=8 EndY=6 EndZ=0
  constraints (14):
    c: Coincident(g0,g-1)
    c: Distance(g0) = 6
    c: Vertical(g0)
    c: Coincident(g3,g0)
    c: Weight(g1) = 1
    c: Equal(g1,g2)
    c: InternalAlignment(g1,g3)
    c: InternalAlignment(g2,g3)
    c: InternalAlignment(g4,g3)
    c: InternalAlignment(g5,g3)
    c: Block(g3)
    c: Coincident(g6,g0)
    c: Coincident(g6,g3)
    c: Horizontal(g6)
FEATURE [Part::Extrusion] Extrude017  label="caseScrewPillarBracket005"
  Base = -> Sketch023
  Dir = (0,0,1)
  DirMode = 2
  FaceMakerClass = Part::FaceMakerBullseye
  LengthFwd = 2.4
  LengthRev = 0
  Placement = pos=(90.7,29,6.77) rot=(0,-1,0;1.5708rad)
  Solid = true
  Symmetric = false
FEATURE [Sketcher::SketchObject] Sketch024
  FullyConstrained = true
  sketch-geometry (7):
    g0: LineSegment StartX=0 StartY=0 StartZ=0 EndX=0 EndY=6 EndZ=0
    g1: Circle CenterX=0 CenterY=0 CenterZ=0 NormalX=0 NormalY=0 NormalZ=1 AngleXU=0 Radius=1
    g2: Circle CenterX=8 CenterY=6 CenterZ=0 NormalX=0 NormalY=0 NormalZ=1 AngleXU=0 Radius=1
    g3: BSplineCurve PolesCount=3 KnotsCount=2 Degree=2 IsPeriodic=0
    g4: GeomPoint X=0 Y=0 Z=0
    g5: GeomPoint X=8 Y=6 Z=0
    g6: LineSegment StartX=0 StartY=6 StartZ=0 EndX=8 EndY=6 EndZ=0
  constraints (14):
    c: Coincident(g0,g-1)
    c: Distance(g0) = 6
    c: Vertical(g0)
    c: Coincident(g3,g0)
    c: Weight(g1) = 1
    c: Equal(g1,g2)
    c: InternalAlignment(g1,g3)
    c: InternalAlignment(g2,g3)
    c: InternalAlignment(g4,g3)
    c: InternalAlignment(g5,g3)
    c: Block(g3)
    c: Coincident(g6,g0)
    c: Coincident(g6,g3)
    c: Horizontal(g6)
FEATURE [Part::Extrusion] Extrude018  label="caseScrewPillarBracket006"
  Base = -> Sketch024
  Dir = (0,0,1)
  DirMode = 2
  FaceMakerClass = Part::FaceMakerBullseye
  LengthFwd = 2.4
  LengthRev = 0
  Placement = pos=(103.7,29,6.77) rot=(0,-1,0;1.5708rad)
  Solid = true
  Symmetric = false
FEATURE [Sketcher::SketchObject] Sketch025
  FullyConstrained = true
  sketch-geometry (7):
    g0: LineSegment StartX=0 StartY=0 StartZ=0 EndX=0 EndY=6 EndZ=0
    g1: Circle CenterX=0 CenterY=0 CenterZ=0 NormalX=0 NormalY=0 NormalZ=1 AngleXU=0 Radius=1
    g2: Circle CenterX=8 CenterY=6 CenterZ=0 NormalX=0 NormalY=0 NormalZ=1 AngleXU=0 Radius=1
    g3: BSplineCurve PolesCount=3 KnotsCount=2 Degree=2 IsPeriodic=0
    g4: GeomPoint X=0 Y=0 Z=0
    g5: GeomPoint X=8 Y=6 Z=0
    g6: LineSegment StartX=0 StartY=6 StartZ=0 EndX=8 EndY=6 EndZ=0
  constraints (14):
    c: Coincident(g0,g-1)
    c: Distance(g0) = 6
    c: Vertical(g0)
    c: Coincident(g3,g0)
    c: Weight(g1) = 1
    c: Equal(g1,g2)
    c: InternalAlignment(g1,g3)
    c: InternalAlignment(g2,g3)
    c: InternalAlignment(g4,g3)
    c: InternalAlignment(g5,g3)
    c: Block(g3)
    c: Coincident(g6,g0)
    c: Coincident(g6,g3)
    c: Horizontal(g6)
FEATURE [Part::Extrusion] Extrude019  label="caseScrewPillarBracket007"
  Base = -> Sketch025
  Dir = (0,0,1)
  DirMode = 2
  FaceMakerClass = Part::FaceMakerBullseye
  LengthFwd = 2.4
  LengthRev = 0
  Placement = pos=(101.3,29,65.23) rot=(0,1,0;1.5708rad)
  Solid = true
  Symmetric = false
FEATURE [Part::Box] Box011  label="frontCaseScrewPillarBracket"
  AttacherType = Attacher::AttachEngine3D
  Height = 2.4
  Length = 16
  Placement = pos=(87,28,2.3) rot=(0,0,1;0rad)
  Width = 7
FEATURE [Part::Box] Box012  label="frontCaseScrewPillarBracket001"
  AttacherType = Attacher::AttachEngine3D
  Height = 2.4
  Length = 16
  Placement = pos=(87,28,67.3) rot=(0,0,1;0rad)
  Width = 7
FEATURE [Sketcher::SketchObject] Sketch026
  FullyConstrained = true
  sketch-geometry (17):
    g0: Circle CenterX=-3.5 CenterY=23.5 CenterZ=0 NormalX=0 NormalY=0 NormalZ=1 AngleXU=0 Radius=1
    g1: Circle CenterX=-1 CenterY=15.25 CenterZ=0 NormalX=0 NormalY=0 NormalZ=1 AngleXU=0 Radius=1
    g2: Circle CenterX=-3.5 CenterY=7 CenterZ=0 NormalX=0 NormalY=0 NormalZ=1 AngleXU=0 Radius=1
    g3: BSplineCurve PolesCount=3 KnotsCount=2 Degree=2 IsPeriodic=0
    g4: GeomPoint X=-3.5 Y=23.5 Z=0
    g5: GeomPoint X=-3.5 Y=7 Z=0
    g6: Circle CenterX=-4.8 CenterY=30.5 CenterZ=0 NormalX=0 NormalY=0 NormalZ=1 AngleXU=0 Radius=1
    g7: Circle CenterX=-3.5 CenterY=30.5 CenterZ=0 NormalX=0 NormalY=0 NormalZ=1 AngleXU=0 Radius=1
    g8: Circle CenterX=-3.5 CenterY=29.2 CenterZ=0 NormalX=0 NormalY=0 NormalZ=1 AngleXU=0 Radius=1
    g9: BSplineCurve PolesCount=3 KnotsCount=2 Degree=2 IsPeriodic=0
    g10: GeomPoint X=-4.8 Y=30.5 Z=0
    g11: GeomPoint X=-3.5 Y=29.2 Z=0
    g12: LineSegment StartX=-3.5 StartY=29.2 StartZ=0 EndX=-3.5 EndY=23.5 EndZ=0
    g13: LineSegment StartX=-4.8 StartY=30.5 StartZ=0 EndX=0 EndY=30.5 EndZ=0
    g14: LineSegment StartX=-3.5 StartY=5 StartZ=0 EndX=-3.5 EndY=7 EndZ=0
    g15: LineSegment StartX=0 StartY=5 StartZ=0 EndX=0 EndY=30.5 EndZ=0
    g16: LineSegment StartX=-3.5 StartY=5 StartZ=0 EndX=0 EndY=5 EndZ=0
  constraints (33):
    c: Weight(g0) = 1
    c: Equal(g0,g1)
    c: Equal(g0,g2)
    c: InternalAlignment(g0,g3)
    c: InternalAlignment(g1,g3)
    c: InternalAlignment(g2,g3)
    c: InternalAlignment(g4,g3)
    c: InternalAlignment(g5,g3)
    c: Block(g3)
    c: Weight(g6) = 1
    c: Equal(g6,g7)
    c: Equal(g6,g8)
    c: InternalAlignment(g6,g9)
    c: InternalAlignment(g7,g9)
    c: InternalAlignment(g8,g9)
    c: InternalAlignment(g10,g9)
    c: InternalAlignment(g11,g9)
    c: Block(g9)
    c: Coincident(g12,g9)
    c: Coincident(g12,g3)
    c: Vertical(g12)
    c: Coincident(g13,g9)
    c: Horizontal(g13)
    c: Distance(g13) = 4.8
    c: Coincident(g14,g3)
    c: Vertical(g14)
    c: Coincident(g15,g13)
    c: Vertical(g15)
    c: Tangent(g15,g1)
    c: Distance(g14) = 2
    c: Coincident(g16,g14)
    c: Horizontal(g16)
    c: Coincident(g15,g16)
FEATURE [Part::Feature] Face050
  shape: bbox 4.8 x 25.5 x 2e-07 mm, 1 faces, 0 solids (baked)
FEATURE [Part::Revolution] Revolve054  label="moreFrontCaseScrewPost001"
  Angle = 360
  Axis = (0,1,0)
  Base = (0,0,0)
  FaceMakerClass = Part::FaceMakerBullseye
  Placement = pos=(102.5,4.5,3.5) rot=(0,0,1;0rad)
  Solid = false
  Source = -> Face050
  Symmetric = false
FEATURE [Part::Feature] Face051
  shape: bbox 4.8 x 25.5 x 2e-07 mm, 1 faces, 0 solids (baked)
FEATURE [Part::Revolution] Revolve055  label="moreFrontCaseScrewPost002"
  Angle = 360
  Axis = (0,1,0)
  Base = (0,0,0)
  FaceMakerClass = Part::FaceMakerBullseye
  Placement = pos=(102.5,4.5,68.5) rot=(0,0,1;0rad)
  Solid = false
  Source = -> Face051
  Symmetric = false
FEATURE [Sketcher::SketchObject] Sketch027
  FullyConstrained = true
  sketch-geometry (10):
    g0: LineSegment StartX=-1.6 StartY=4.7 StartZ=0 EndX=-1.6 EndY=1.7 EndZ=0
    g1: LineSegment StartX=-3.5 StartY=4.7 StartZ=0 EndX=-1.6 EndY=4.7 EndZ=0
    g2: LineSegment StartX=-1.6 StartY=1.7 StartZ=0 EndX=-1.6 EndY=1.5 EndZ=0
    g3: LineSegment StartX=-1.6 StartY=1.5 StartZ=0 EndX=-5.2 EndY=1.5 EndZ=0
    g4: Circle CenterX=-3.5 CenterY=4.7 CenterZ=0 NormalX=0 NormalY=0 NormalZ=1 AngleXU=0 Radius=1
    g5: Circle CenterX=-3.59627 CenterY=2.99743 CenterZ=0 NormalX=0 NormalY=0 NormalZ=1 AngleXU=0 Radius=1
    g6: Circle CenterX=-5.2 CenterY=1.5 CenterZ=0 NormalX=0 NormalY=0 NormalZ=1 AngleXU=0 Radius=1
    g7: BSplineCurve PolesCount=3 KnotsCount=2 Degree=2 IsPeriodic=0
    g8: GeomPoint X=-3.5 Y=4.7 Z=0
    g9: GeomPoint X=-5.2 Y=1.5 Z=0
  constraints (23):
    c: Vertical(g0)
    c: Distance(g0) = 3
    c: Coincident(g1,g0)
    c: Horizontal(g1)
    c: Block(g0)
    c: Block(g1)
    c: Coincident(g2,g0)
    c: Vertical(g2)
    c: Distance(g2) = 0.2
    c: Coincident(g3,g2)
    c: Horizontal(g3)
    c: Block(g3)
    c: Coincident(g7,g1)
    c: Weight(g4) = 1
    c: Equal(g4,g5)
    c: Equal(g4,g6)
    c: Coincident(g7,g3)
    c: InternalAlignment(g4,g7)
    c: InternalAlignment(g5,g7)
    c: InternalAlignment(g6,g7)
    c: InternalAlignment(g8,g7)
    c: InternalAlignment(g9,g7)
    c: Block(g7)
FEATURE [Sketcher::SketchObject] Sketch028
  FullyConstrained = true
  sketch-geometry (18):
    g0: LineSegment StartX=0 StartY=3e-16 StartZ=0 EndX=0 EndY=1.7 EndZ=0
    g1: LineSegment StartX=-3.5 StartY=0 StartZ=0 EndX=-3.5 EndY=0.9 EndZ=0
    g2: Circle CenterX=-2.7 CenterY=1.7 CenterZ=0 NormalX=0 NormalY=0 NormalZ=1 AngleXU=0 Radius=1
    g3: Circle CenterX=-3.5 CenterY=1.7 CenterZ=0 NormalX=0 NormalY=0 NormalZ=1 AngleXU=0 Radius=1
    g4: Circle CenterX=-3.5 CenterY=0.9 CenterZ=0 NormalX=0 NormalY=0 NormalZ=1 AngleXU=0 Radius=1
    g5: BSplineCurve PolesCount=3 KnotsCount=2 Degree=2 IsPeriodic=0
    g6: GeomPoint X=-2.7 Y=1.7 Z=0
    g7: GeomPoint X=-3.5 Y=0.9 Z=0
    g8: LineSegment StartX=-3.5 StartY=0 StartZ=0 EndX=-3.5 EndY=-7 EndZ=0
    g9: LineSegment StartX=0 StartY=3e-16 StartZ=0 EndX=0 EndY=-7 EndZ=0
    g10: LineSegment StartX=-3.5 StartY=-7 StartZ=0 EndX=0 EndY=-7 EndZ=0
    g11: LineSegment StartX=-2.7 StartY=1.7 StartZ=0 EndX=-1.6 EndY=1.7 EndZ=0
    g12: LineSegment StartX=0 StartY=1.7 StartZ=0 EndX=0 EndY=4.5 EndZ=0
    g13: LineSegment StartX=0 StartY=4.5 StartZ=0 EndX=0 EndY=10.8 EndZ=0
    g14: LineSegment StartX=0 StartY=10.8 StartZ=0 EndX=-2 EndY=10.8 EndZ=0
    g15: LineSegment StartX=-1.6 StartY=4.7 StartZ=0 EndX=-1.6 EndY=1.7 EndZ=0
    g16: LineSegment StartX=-1.6 StartY=4.7 StartZ=0 EndX=-2 EndY=4.7 EndZ=0
    g17: LineSegment StartX=-2 StartY=4.7 StartZ=0 EndX=-2 EndY=10.8 EndZ=0
  constraints (44):
    c: Vertical(g0)
    c: Vertical(g1)
    c: Distance(g1) = 0.9
    c: Block(g0)
    c: Distance(g0) = 1.7
    c: Weight(g2) = 1
    c: Equal(g2,g3)
    c: Equal(g2,g4)
    c: Coincident(g5,g1)
    c: InternalAlignment(g2,g5)
    c: InternalAlignment(g3,g5)
    c: InternalAlignment(g4,g5)
    c: InternalAlignment(g6,g5)
    c: InternalAlignment(g7,g5)
    c: Block(g5)
    c: Coincident(g8,g1)
    c: Vertical(g8)
    c: Distance(g8) = 7
    c: Vertical(g9)
    c: Equal(g8,g9) = 7
    c: Coincident(g9,g0)
    c: Coincident(g10,g8)
    c: Coincident(g10,g9)
    c: Horizontal(g10)
    c: Coincident(g11,g5)
    c: Horizontal(g11)
    c: Coincident(g12,g0)
    c: Vertical(g12)
    c: Distance(g12) = 2.8
    c: Coincident(g13,g12)
    c: Vertical(g13)
    c: Distance(g13) = 6.3
    c: Coincident(g14,g13)
    c: Horizontal(g14)
    c: Distance(g14) = 2
    c: Vertical(g15)
    c: Distance(g15) = 3
    c: Block(g11)
    c: Coincident(g15,g11)
    c: Coincident(g16,g15)
    c: Horizontal(g16)
    c: Coincident(g17,g16)
    c: Coincident(g17,g14)
    c: Vertical(g17)
FEATURE [Part::Revolution] Revolve040  label="backCaseScrewRetainer001"
  Angle = 360
  Axis = (0,1,0)
  Base = (0,0,0)
  FaceMakerClass = Part::FaceMakerBullseye
  Placement = pos=(12.5,3,10) rot=(0,0,1;0rad)
  Solid = false
  Source = -> Face036
  Symmetric = false
FEATURE [Part::Feature] Face055
  shape: bbox 3.5 x 30.2 x 2e-07 mm, 1 faces, 0 solids (baked)
FEATURE [Part::Revolution] Revolve059  label="backCaseScrewPost"
  Angle = 360
  Axis = (0,1,0)
  Base = (0,0,0)
  FaceMakerClass = Part::FaceMakerBullseye
  Placement = pos=(12.5,4.5,10) rot=(0,0,1;0rad)
  Solid = false
  Source = -> Face055
  Symmetric = false
FEATURE [Part::Feature] Face056
  shape: bbox 3.5 x 30.2 x 2e-07 mm, 1 faces, 0 solids (baked)
FEATURE [Part::Revolution] Revolve060  label="backCaseScrewPost001"
  Angle = 360
  Axis = (0,1,0)
  Base = (0,0,0)
  FaceMakerClass = Part::FaceMakerBullseye
  Placement = pos=(12.5,4.5,62) rot=(0,0,1;0rad)
  Solid = false
  Source = -> Face056
  Symmetric = false
FEATURE [Part::Feature] Face057
  shape: bbox 3.5 x 17.8 x 2e-07 mm, 1 faces, 0 solids (baked)
FEATURE [Part::Revolution] Revolve061  label="removeToCreateScrewAndThreadedInsertHole"
  Angle = 360
  Axis = (0,1,0)
  Base = (0,0,0)
  FaceMakerClass = Part::FaceMakerBullseye
  Placement = pos=(12.5,0,10) rot=(0,0,1;0rad)
  Solid = false
  Source = -> Face057
  Symmetric = false
FEATURE [Part::Feature] Face058
  shape: bbox 3.5 x 17.8 x 2e-07 mm, 1 faces, 0 solids (baked)
FEATURE [Part::Revolution] Revolve062  label="removeToCreateScrewAndThreadedInsertHole001"
  Angle = 360
  Axis = (0,1,0)
  Base = (0,0,0)
  FaceMakerClass = Part::FaceMakerBullseye
  Placement = pos=(12.5,0,62) rot=(0,0,1;0rad)
  Solid = false
  Source = -> Face058
  Symmetric = false
FEATURE [Part::Feature] Face059
  shape: bbox 3.5 x 17.8 x 2e-07 mm, 1 faces, 0 solids (baked)
FEATURE [Part::Revolution] Revolve063  label="removeToCreateScrewAndThreadedInsertHole002"
  Angle = 360
  Axis = (0,1,0)
  Base = (0,0,0)
  FaceMakerClass = Part::FaceMakerBullseye
  Placement = pos=(89.5,0,68.5) rot=(0,0,1;0rad)
  Solid = false
  Source = -> Face059
  Symmetric = false
FEATURE [Part::Feature] Face060
  shape: bbox 3.5 x 17.8 x 2e-07 mm, 1 faces, 0 solids (baked)
FEATURE [Part::Revolution] Revolve064  label="removeToCreateScrewAndThreadedInsertHole003"
  Angle = 360
  Axis = (0,1,0)
  Base = (0,0,0)
  FaceMakerClass = Part::FaceMakerBullseye
  Placement = pos=(89.5,0,3.5) rot=(0,0,1;0rad)
  Solid = false
  Source = -> Face060
  Symmetric = false
FEATURE [Part::Feature] Face061
  shape: bbox 3.5 x 17.8 x 2e-07 mm, 1 faces, 0 solids (baked)
FEATURE [Part::Revolution] Revolve065  label="removeToCreateScrewAndThreadedInsertHole004"
  Angle = 360
  Axis = (0,1,0)
  Base = (0,0,0)
  FaceMakerClass = Part::FaceMakerBullseye
  Placement = pos=(102.5,4.7,3.5) rot=(0,0,1;0rad)
  Solid = false
  Source = -> Face061
  Symmetric = false
FEATURE [Part::Feature] Face062
  shape: bbox 3.5 x 17.8 x 2e-07 mm, 1 faces, 0 solids (baked)
FEATURE [Part::Revolution] Revolve066  label="removeToCreateScrewAndThreadedInsertHole005"
  Angle = 360
  Axis = (0,1,0)
  Base = (0,0,0)
  FaceMakerClass = Part::FaceMakerBullseye
  Placement = pos=(102.5,4.7,68.5) rot=(0,0,1;0rad)
  Solid = false
  Source = -> Face062
  Symmetric = false
FEATURE [Part::MultiFuse] Fusion047  label="makeHoles"
  Shapes = -> [Revolve066,Revolve065,Revolve064,Revolve063,Revolve062,Revolve061]
FEATURE [Part::Feature] Face063
  shape: bbox 3.6 x 3.2 x 2e-07 mm, 1 faces, 0 solids (baked)
FEATURE [Part::Revolution] Revolve067  label="moreFrontCaseScrewRetainer002"
  Angle = 360
  Axis = (0,1,0)
  Base = (0,0,0)
  FaceMakerClass = Part::FaceMakerBullseye
  Placement = pos=(102.5,4.5,68.5) rot=(0,0,1;0rad)
  Solid = false
  Source = -> Face063
  Symmetric = false
FEATURE [Part::Feature] Face064
  shape: bbox 3.6 x 3.2 x 2e-07 mm, 1 faces, 0 solids (baked)
FEATURE [Part::Revolution] Revolve068  label="moreFrontCaseScrewRetainer003"
  Angle = 360
  Axis = (0,1,0)
  Base = (0,0,0)
  FaceMakerClass = Part::FaceMakerBullseye
  Placement = pos=(102.5,4.5,3.5) rot=(0,0,1;0rad)
  Solid = false
  Source = -> Face064
  Symmetric = false
FEATURE [Part::Feature] Face065
  shape: bbox 3.5 x 17.8 x 2e-07 mm, 1 faces, 0 solids (baked)
FEATURE [Part::Revolution] Revolve069  label="removeToCreateScrewAndThreadedInsertHole006"
  Angle = 360
  Axis = (0,1,0)
  Base = (0,0,0)
  FaceMakerClass = Part::FaceMakerBullseye
  Placement = pos=(12.5,0,10) rot=(0,0,1;0rad)
  Solid = false
  Source = -> Face065
  Symmetric = false
FEATURE [Part::Feature] Face066
  shape: bbox 3.5 x 17.8 x 2e-07 mm, 1 faces, 0 solids (baked)
FEATURE [Part::Revolution] Revolve070  label="removeToCreateScrewAndThreadedInsertHole007"
  Angle = 360
  Axis = (0,1,0)
  Base = (0,0,0)
  FaceMakerClass = Part::FaceMakerBullseye
  Placement = pos=(12.5,0,62) rot=(0,0,1;0rad)
  Solid = false
  Source = -> Face066
  Symmetric = false
FEATURE [Part::Feature] Face067
  shape: bbox 3.5 x 17.8 x 2e-07 mm, 1 faces, 0 solids (baked)
FEATURE [Part::Revolution] Revolve071  label="removeToCreateScrewAndThreadedInsertHole008"
  Angle = 360
  Axis = (0,1,0)
  Base = (0,0,0)
  FaceMakerClass = Part::FaceMakerBullseye
  Placement = pos=(89.5,0,68.5) rot=(0,0,1;0rad)
  Solid = false
  Source = -> Face067
  Symmetric = false
FEATURE [Part::Feature] Face068
  shape: bbox 3.5 x 17.8 x 2e-07 mm, 1 faces, 0 solids (baked)
FEATURE [Part::Revolution] Revolve072  label="removeToCreateScrewAndThreadedInsertHole009"
  Angle = 360
  Axis = (0,1,0)
  Base = (0,0,0)
  FaceMakerClass = Part::FaceMakerBullseye
  Placement = pos=(89.5,0,3.5) rot=(0,0,1;0rad)
  Solid = false
  Source = -> Face068
  Symmetric = false
FEATURE [Part::Feature] Face069
  shape: bbox 3.5 x 17.8 x 2e-07 mm, 1 faces, 0 solids (baked)
FEATURE [Part::Feature] Face070
  shape: bbox 3.5 x 17.8 x 2e-07 mm, 1 faces, 0 solids (baked)
FEATURE [Part::Revolution] Revolve073  label="removeToCreateScrewAndThreadedInsertHole010"
  Angle = 360
  Axis = (0,1,0)
  Base = (0,0,0)
  FaceMakerClass = Part::FaceMakerBullseye
  Placement = pos=(102.5,4.7,3.5) rot=(0,0,1;0rad)
  Solid = false
  Source = -> Face069
  Symmetric = false
FEATURE [Part::Revolution] Revolve074  label="removeToCreateScrewAndThreadedInsertHole011"
  Angle = 360
  Axis = (0,1,0)
  Base = (0,0,0)
  FaceMakerClass = Part::FaceMakerBullseye
  Placement = pos=(102.5,4.7,68.5) rot=(0,0,1;0rad)
  Solid = false
  Source = -> Face070
  Symmetric = false
FEATURE [Part::MultiFuse] Fusion048  label="makeHoles001"
  Shapes = -> [Revolve074,Revolve073,Revolve072,Revolve071,Revolve070,Revolve069]
FEATURE [Part::MultiFuse] Fusion049  label="caseScrewRetainers"
  Shapes = -> [Revolve067,Revolve068,Revolve048,Revolve047,Revolve039,Revolve040]
FEATURE [Part::Cut] Cut015  label="caseScrewRetainers001"
  Base = -> Fusion049
  Tool = -> Fusion048
FEATURE [Part::MultiFuse] Fusion050  label="casePillars"
  Shapes = -> [Revolve055,Revolve054,Revolve043,Revolve046,Revolve059,Revolve060]
FEATURE [Part::Feature] Face071 .. Face076  x6 (patterned run collapsed; names and placements below)
  shape: bbox 3.5 x 17.8 x 2e-07 mm, 1 faces, 0 solids (baked)
FEATURE [Part::Revolution] Revolve075  label="removeToCreateScrewAndThreadedInsertHole012"
  Angle = 360
  Axis = (0,1,0)
  Base = (0,0,0)
  FaceMakerClass = Part::FaceMakerBullseye
  Placement = pos=(12.5,0,10) rot=(0,0,1;0rad)
  Solid = false
  Source = -> Face071
  Symmetric = false
FEATURE [Part::Revolution] Revolve076  label="removeToCreateScrewAndThreadedInsertHole013"
  Angle = 360
  Axis = (0,1,0)
  Base = (0,0,0)
  FaceMakerClass = Part::FaceMakerBullseye
  Placement = pos=(12.5,0,62) rot=(0,0,1;0rad)
  Solid = false
  Source = -> Face072
  Symmetric = false
FEATURE [Part::Revolution] Revolve077  label="removeToCreateScrewAndThreadedInsertHole014"
  Angle = 360
  Axis = (0,1,0)
  Base = (0,0,0)
  FaceMakerClass = Part::FaceMakerBullseye
  Placement = pos=(89.5,0,68.5) rot=(0,0,1;0rad)
  Solid = false
  Source = -> Face073
  Symmetric = false
FEATURE [Part::Revolution] Revolve078  label="removeToCreateScrewAndThreadedInsertHole015"
  Angle = 360
  Axis = (0,1,0)
  Base = (0,0,0)
  FaceMakerClass = Part::FaceMakerBullseye
  Placement = pos=(89.5,0,3.5) rot=(0,0,1;0rad)
  Solid = false
  Source = -> Face074
  Symmetric = false
FEATURE [Part::Revolution] Revolve079  label="removeToCreateScrewAndThreadedInsertHole016"
  Angle = 360
  Axis = (0,1,0)
  Base = (0,0,0)
  FaceMakerClass = Part::FaceMakerBullseye
  Placement = pos=(102.5,4.7,3.5) rot=(0,0,1;0rad)
  Solid = false
  Source = -> Face075
  Symmetric = false
FEATURE [Part::Revolution] Revolve080  label="removeToCreateScrewAndThreadedInsertHole017"
  Angle = 360
  Axis = (0,1,0)
  Base = (0,0,0)
  FaceMakerClass = Part::FaceMakerBullseye
  Placement = pos=(102.5,4.7,68.5) rot=(0,0,1;0rad)
  Solid = false
  Source = -> Face076
  Symmetric = false
FEATURE [Part::MultiFuse] Fusion051  label="makeHoles002"
  Shapes = -> [Revolve080,Revolve079,Revolve078,Revolve077,Revolve076,Revolve075]
FEATURE [Part::Cut] Cut016  label="caesPillars"
  Base = -> Fusion050
  Tool = -> Fusion051
FEATURE [Part::Revolution] Revolve009  label="plugHousing016"
  Angle = 360
  Axis = (0,1,0)
  Base = (0,0,0)
  FaceMakerClass = Part::FaceMakerBullseye
  Placement = pos=(0,0,36.15) rot=(0,0,1;0rad)
  Solid = false
  Source = -> Face012
  Symmetric = false
FEATURE [Part::MultiFuse] Fusion014  label="plugHousing023"
  Placement = pos=(0,0,0) rot=(0,0,1;1.5708rad)
  Shapes = -> [Revolve011,Revolve009]
FEATURE [Part::Revolution] Revolve010  label="plugHousing017"
  Angle = 360
  Axis = (0,1,0)
  Base = (0,0,0)
  FaceMakerClass = Part::FaceMakerBullseye
  Placement = pos=(0,0,36.15) rot=(0,0,1;0rad)
  Solid = false
  Source = -> Face014
  Symmetric = false
FEATURE [Part::MultiFuse] Fusion015  label="plugHousing024"
  Placement = pos=(0,0,0) rot=(0,0,1;1.5708rad)
  Shapes = -> [Revolve010,Revolve015]
FEATURE [Part::Revolution] Revolve014  label="plugHousing026"
  Angle = 360
  Axis = (0,1,0)
  Base = (0,0,0)
  FaceMakerClass = Part::FaceMakerBullseye
  Placement = pos=(0,0,36.15) rot=(0,0,1;0rad)
  Solid = false
  Source = -> Face011
  Symmetric = false
FEATURE [Part::Revolution] Revolve013  label="plugHousing025"
  Angle = 360
  Axis = (0,1,0)
  Base = (0,0,0)
  FaceMakerClass = Part::FaceMakerBullseye
  Placement = pos=(0,0,36.15) rot=(0,0,1;0rad)
  Solid = false
  Source = -> Face015
  Symmetric = false
FEATURE [Part::MultiFuse] Fusion016  label="plugHousing028"
  Placement = pos=(0,19,0) rot=(0,0,1;3.14159rad)
  Shapes = -> [Fusion014,Fusion013]
FEATURE [Part::MultiFuse] Fusion011  label="plugHousing018"
  Placement = pos=(0,0,0) rot=(0,0,1;1.5708rad)
  Shapes = -> [Revolve014,Revolve013]
FEATURE [Part::MultiFuse] Fusion012  label="plugHousing019"
  Placement = pos=(0,19,0) rot=(0,0,1;3.14159rad)
  Shapes = -> [Fusion011,Fusion015]
FEATURE [Part::MultiFuse] Fusion017  label="plugHousing029"
  Placement = pos=(122.621,0,-0.15) rot=(0,0,1;0rad)
  Shapes = -> [Fusion016,Fusion012]
FEATURE [Part::MultiFuse] Fusion052  label="casePillarRetainers"
  Shapes = -> [Extrude012,Extrude013,Extrude014,Extrude015,Extrude016,Extrude017,Extrude018,Extrude019,Box011,Box012]
FEATURE [Part::Feature] Face077
  shape: bbox 3.5 x 17.8 x 2e-07 mm, 1 faces, 0 solids (baked)
FEATURE [Part::Revolution] Revolve081  label="removeToCreateScrewAndThreadedInsertHole018"
  Angle = 360
  Axis = (0,1,0)
  Base = (0,0,0)
  FaceMakerClass = Part::FaceMakerBullseye
  Placement = pos=(62.3,30.3,19.7) rot=(0,0,1;0rad)
  Solid = false
  Source = -> Face077
  Symmetric = false
FEATURE [Part::Feature] Face078
  shape: bbox 3.5 x 17.8 x 2e-07 mm, 1 faces, 0 solids (baked)
FEATURE [Part::Revolution] Revolve082  label="removeToCreateScrewAndThreadedInsertHole019"
  Angle = 360
  Axis = (0,1,0)
  Base = (0,0,0)
  FaceMakerClass = Part::FaceMakerBullseye
  Placement = pos=(62.3,30.3,51.7) rot=(0,0,1;0rad)
  Solid = false
  Source = -> Face078
  Symmetric = false
FEATURE [Part::Feature] Face079
  shape: bbox 3.5 x 17.8 x 2e-07 mm, 1 faces, 0 solids (baked)
FEATURE [Part::Revolution] Revolve083  label="removeToCreateScrewAndThreadedInsertHole020"
  Angle = 360
  Axis = (0,1,0)
  Base = (0,0,0)
  FaceMakerClass = Part::FaceMakerBullseye
  Placement = pos=(30.3,30.3,19.7) rot=(0,0,1;0rad)
  Solid = false
  Source = -> Face079
  Symmetric = false
FEATURE [Part::Feature] Face080
  shape: bbox 3.5 x 17.8 x 2e-07 mm, 1 faces, 0 solids (baked)
FEATURE [Part::Revolution] Revolve084  label="removeToCreateScrewAndThreadedInsertHole021"
  Angle = 360
  Axis = (0,1,0)
  Base = (0,0,0)
  FaceMakerClass = Part::FaceMakerBullseye
  Placement = pos=(30.3,30.3,51.7) rot=(0,0,1;0rad)
  Solid = false
  Source = -> Face080
  Symmetric = false
FEATURE [Part::MultiFuse] Fusion053  label="createThreadedInsertHolesForFan"
  Shapes = -> [Revolve081,Revolve082,Revolve083,Revolve084]
FEATURE [Part::Cut] Cut017  label="fanScrewHousing001"
  Base = -> Fusion046
  Tool = -> Fusion053
FEATURE [Part::Feature] Face081
  shape: bbox 3.5 x 17.8 x 2e-07 mm, 1 faces, 0 solids (baked)
FEATURE [Part::Revolution] Revolve085  label="removeToCreateScrewAndThreadedInsertHole022"
  Angle = 360
  Axis = (0,1,0)
  Base = (0,0,0)
  FaceMakerClass = Part::FaceMakerBullseye
  Placement = pos=(62.3,30.3,19.7) rot=(0,0,1;0rad)
  Solid = false
  Source = -> Face081
  Symmetric = false
FEATURE [Part::Feature] Face082
  shape: bbox 3.5 x 17.8 x 2e-07 mm, 1 faces, 0 solids (baked)
FEATURE [Part::Revolution] Revolve086  label="removeToCreateScrewAndThreadedInsertHole023"
  Angle = 360
  Axis = (0,1,0)
  Base = (0,0,0)
  FaceMakerClass = Part::FaceMakerBullseye
  Placement = pos=(62.3,30.3,51.7) rot=(0,0,1;0rad)
  Solid = false
  Source = -> Face082
  Symmetric = false
FEATURE [Part::Feature] Face083
  shape: bbox 3.5 x 17.8 x 2e-07 mm, 1 faces, 0 solids (baked)
FEATURE [Part::Revolution] Revolve087  label="removeToCreateScrewAndThreadedInsertHole024"
  Angle = 360
  Axis = (0,1,0)
  Base = (0,0,0)
  FaceMakerClass = Part::FaceMakerBullseye
  Placement = pos=(30.3,30.3,19.7) rot=(0,0,1;0rad)
  Solid = false
  Source = -> Face083
  Symmetric = false
FEATURE [Part::Feature] Face084
  shape: bbox 3.5 x 17.8 x 2e-07 mm, 1 faces, 0 solids (baked)
FEATURE [Part::Revolution] Revolve088  label="removeToCreateScrewAndThreadedInsertHole025"
  Angle = 360
  Axis = (0,1,0)
  Base = (0,0,0)
  FaceMakerClass = Part::FaceMakerBullseye
  Placement = pos=(30.3,30.3,51.7) rot=(0,0,1;0rad)
  Solid = false
  Source = -> Face084
  Symmetric = false
FEATURE [Part::MultiFuse] Fusion054  label="createThreadedInsertHolesForFan001"
  Shapes = -> [Revolve085,Revolve086,Revolve087,Revolve088]
FEATURE [Part::Cut] Cut018  label="top007"
  Base = -> Fusion040
  Tool = -> Fusion054
FEATURE [Sketcher::SketchObject] Sketch029
  FullyConstrained = false
  Placement = pos=(0,0,0) rot=(1,0,0;1.5708rad)
  sketch-geometry (24):
    g0: ArcOfCircle CenterX=-4 CenterY=-10.5 CenterZ=0 NormalX=0 NormalY=0 NormalZ=1 AngleXU=0 Radius=1.5 StartAngle=6e-16 EndAngle=3.14159
    g1: ArcOfCircle CenterX=-34.2 CenterY=-10.5 CenterZ=0 NormalX=0 NormalY=0 NormalZ=1 AngleXU=0 Radius=1.5 StartAngle=0 EndAngle=3.14159
    g2: ArcOfCircle CenterX=-34.2 CenterY=-27.7 CenterZ=0 NormalX=0 NormalY=0 NormalZ=1 AngleXU=0 Radius=1.5 StartAngle=3.14159 EndAngle=6.28319
    g3: ArcOfCircle CenterX=-4 CenterY=-27.7 CenterZ=0 NormalX=0 NormalY=0 NormalZ=1 AngleXU=0 Radius=1.5 StartAngle=3.1416 EndAngle=6.28319
    g4: ArcOfCircle CenterX=-10 CenterY=-4.3 CenterZ=0 NormalX=0 NormalY=0 NormalZ=1 AngleXU=0 Radius=1.5 StartAngle=2e-16 EndAngle=3.14159
    g5: ArcOfCircle CenterX=-16.1 CenterY=-1.8 CenterZ=0 NormalX=0 NormalY=0 NormalZ=1 AngleXU=0 Radius=1.5 StartAngle=5e-16 EndAngle=3.14159
    g6: ArcOfCircle CenterX=-22.1 CenterY=-1.8 CenterZ=0 NormalX=0 NormalY=0 NormalZ=1 AngleXU=0 Radius=1.5 StartAngle=5e-16 EndAngle=3.14159
    g7: ArcOfCircle CenterX=-28.2 CenterY=-4.3 CenterZ=0 NormalX=0 NormalY=0 NormalZ=1 AngleXU=0 Radius=1.5 StartAngle=2e-16 EndAngle=3.14159
    g8: ArcOfCircle CenterX=-10 CenterY=-33.9 CenterZ=0 NormalX=0 NormalY=0 NormalZ=1 AngleXU=0 Radius=1.5 StartAngle=3.14159 EndAngle=6.28319
    g9: ArcOfCircle CenterX=-16.1 CenterY=-36.4 CenterZ=0 NormalX=0 NormalY=0 NormalZ=1 AngleXU=0 Radius=1.5 StartAngle=3.14159 EndAngle=6.28319
    g10: ArcOfCircle CenterX=-22.1 CenterY=-36.4 CenterZ=0 NormalX=0 NormalY=0 NormalZ=1 AngleXU=0 Radius=1.5 StartAngle=3.14159 EndAngle=6.28319
    g11: ArcOfCircle CenterX=-28.2 CenterY=-33.9 CenterZ=0 NormalX=0 NormalY=0 NormalZ=1 AngleXU=0 Radius=1.5 StartAngle=3.14159 EndAngle=6.28319
    g12: LineSegment StartX=-35.7 StartY=-10.5 StartZ=0 EndX=-35.7 EndY=-27.7 EndZ=0
    g13: LineSegment StartX=-32.7 StartY=-10.5 StartZ=0 EndX=-32.7 EndY=-27.7 EndZ=0
    g14: LineSegment StartX=-29.7 StartY=-33.9 StartZ=0 EndX=-29.7 EndY=-4.3 EndZ=0
    g15: LineSegment StartX=-26.7 StartY=-33.9 StartZ=0 EndX=-26.7 EndY=-4.3 EndZ=0
    g16: LineSegment StartX=-2.5 StartY=-10.5 StartZ=0 EndX=-2.5 EndY=-27.7 EndZ=0
    g17: LineSegment StartX=-8.5 StartY=-4.3 StartZ=0 EndX=-8.5 EndY=-33.9 EndZ=0
    g18: LineSegment StartX=-5.5 StartY=-10.5 StartZ=0 EndX=-5.5 EndY=-27.7 EndZ=0
    g19: LineSegment StartX=-11.5 StartY=-4.3 StartZ=0 EndX=-11.5 EndY=-33.9 EndZ=0
    g20: LineSegment StartX=-14.6 StartY=-1.8 StartZ=0 EndX=-14.6 EndY=-36.4 EndZ=0
    g21: LineSegment StartX=-17.6 StartY=-1.8 StartZ=0 EndX=-17.6 EndY=-36.4 EndZ=0
    g22: LineSegment StartX=-20.6 StartY=-36.4 StartZ=0 EndX=-20.6 EndY=-1.8 EndZ=0
    g23: LineSegment StartX=-23.6 StartY=-1.8 StartZ=0 EndX=-23.6 EndY=-36.4 EndZ=0
  constraints (48):
    c: Block(g0)
    c: Block(g1)
    c: Block(g2)
    c: Block(g3)
    c: Block(g4)
    c: Block(g5)
    c: Block(g6)
    c: Block(g7)
    c: Block(g8)
    c: Block(g9)
    c: Block(g10)
    c: Block(g11)
    c: Coincident(g12,g1)
    c: Coincident(g12,g2)
    c: Vertical(g12)
    c: Coincident(g13,g1)
    c: Coincident(g13,g2)
    c: Vertical(g13)
    c: Coincident(g14,g11)
    c: Coincident(g14,g7)
    c: Vertical(g14)
    c: Coincident(g15,g11)
    c: Coincident(g15,g7)
    c: Vertical(g15)
    c: Coincident(g16,g0)
    c: Coincident(g16,g3)
    c: Vertical(g16)
    c: Coincident(g17,g4)
    c: Coincident(g17,g8)
    c: Vertical(g17)
    c: Coincident(g18,g0)
    c: Coincident(g18,g3)
    c: Vertical(g18)
    c: Coincident(g19,g4)
    c: Coincident(g19,g8)
    c: Vertical(g19)
    c: Coincident(g20,g5)
    c: Coincident(g20,g9)
    c: Vertical(g20)
    c: Coincident(g21,g5)
    c: Coincident(g21,g9)
    c: Vertical(g21)
    c: Coincident(g22,g10)
    c: Coincident(g22,g6)
    c: Vertical(g22)
    c: Coincident(g23,g6)
    c: Coincident(g23,g10)
    c: Vertical(g23)
FEATURE [Part::Extrusion] Extrude020  label="removeToCreateFanGrillHoles"
  Base = -> Sketch029
  Dir = (0,-1,6e-16)
  DirMode = 2
  FaceMakerClass = Part::FaceMakerBullseye
  LengthFwd = 10
  LengthRev = 0
  Placement = pos=(65.4,44,54.82) rot=(0,0,1;0rad)
  Solid = true
  Symmetric = false
FEATURE [Part::MultiFuse] Fusion055  label="top008"
  Shapes = -> [Cut017,Cut018]
FEATURE [Part::Cut] Cut019  label="top009"
  Base = -> Fusion055
  Tool = -> Extrude020
FEATURE [App::MeasureDistance] Distance003  label="Distance: 71.95 mm"
  Distance = 71.9513
  P1 = (117,38,72)
  P2 = (117,38,0.0487319)
FEATURE [Sketcher::SketchObject] Sketch030
  FullyConstrained = true
  Placement = pos=(117,19,0) rot=(0.57735,0.57735,0.57735;2.0944rad)
  sketch-geometry (48):
    g0: LineSegment StartX=-49.19 StartY=69.25 StartZ=0 EndX=-49.19 EndY=66.25 EndZ=0
    g1: LineSegment StartX=-49.19 StartY=63.5 StartZ=0 EndX=-49.19 EndY=60.5 EndZ=0
    g2: LineSegment StartX=-49.19 StartY=57.75 StartZ=0 EndX=-49.19 EndY=54.75 EndZ=0
    g3: LineSegment StartX=-49.19 StartY=52 StartZ=0 EndX=-49.19 EndY=49 EndZ=0
    g4: LineSegment StartX=-49.19 StartY=46.25 StartZ=0 EndX=-49.19 EndY=43.25 EndZ=0
    g5: LineSegment StartX=-49.19 StartY=40.5 StartZ=0 EndX=-49.19 EndY=37.5 EndZ=0
    g6: LineSegment StartX=-49.19 StartY=34.5 StartZ=0 EndX=-49.19 EndY=31.5 EndZ=0
    g7: LineSegment StartX=-49.19 StartY=28.75 StartZ=0 EndX=-49.19 EndY=25.75 EndZ=0
    g8: LineSegment StartX=-49.19 StartY=23 StartZ=0 EndX=-49.19 EndY=20 EndZ=0
    g9: LineSegment StartX=-49.19 StartY=17.25 StartZ=0 EndX=-49.19 EndY=14.25 EndZ=0
    g10: LineSegment StartX=-49.19 StartY=11.5 StartZ=0 EndX=-49.19 EndY=8.5 EndZ=0
    g11: LineSegment StartX=-49.19 StartY=5.75 StartZ=0 EndX=-49.19 EndY=2.75 EndZ=0
    g12: ArcOfCircle CenterX=-1.5 CenterY=67.75 CenterZ=0 NormalX=0 NormalY=0 NormalZ=1 AngleXU=0 Radius=1.5 StartAngle=4.71239 EndAngle=7.85398
    g13: ArcOfCircle CenterX=-1.5 CenterY=62 CenterZ=0 NormalX=0 NormalY=0 NormalZ=1 AngleXU=0 Radius=1.5 StartAngle=4.71239 EndAngle=7.85398
    g14: ArcOfCircle CenterX=-1.5 CenterY=56.25 CenterZ=0 NormalX=0 NormalY=0 NormalZ=1 AngleXU=0 Radius=1.5 StartAngle=4.71239 EndAngle=7.85398
    g15: ArcOfCircle CenterX=-11.49 CenterY=50.5 CenterZ=0 NormalX=0 NormalY=0 NormalZ=1 AngleXU=0 Radius=1.5 StartAngle=4.71239 EndAngle=7.85398
    g16: ArcOfCircle CenterX=-16.28 CenterY=44.75 CenterZ=0 NormalX=0 NormalY=0 NormalZ=1 AngleXU=0 Radius=1.5 StartAngle=4.71239 EndAngle=7.85398
    g17: ArcOfCircle CenterX=-18.2337 CenterY=39 CenterZ=0 NormalX=0 NormalY=0 NormalZ=1 AngleXU=0 Radius=1.5 StartAngle=4.71485 EndAngle=7.85398
    g18: ArcOfCircle CenterX=-16.2837 CenterY=27.25 CenterZ=0 NormalX=0 NormalY=0 NormalZ=1 AngleXU=0 Radius=1.5 StartAngle=4.71485 EndAngle=7.85398
    g19: ArcOfCircle CenterX=-18.2337 CenterY=33 CenterZ=0 NormalX=0 NormalY=0 NormalZ=1 AngleXU=0 Radius=1.5 StartAngle=4.71485 EndAngle=7.85398
    g20: ArcOfCircle CenterX=-11.49 CenterY=21.5 CenterZ=0 NormalX=0 NormalY=0 NormalZ=1 AngleXU=0 Radius=1.5 StartAngle=4.71239 EndAngle=7.85398
    g21: ArcOfCircle CenterX=-1.5 CenterY=4.25 CenterZ=0 NormalX=0 NormalY=0 NormalZ=1 AngleXU=0 Radius=1.5 StartAngle=4.71239 EndAngle=7.85398
    g22: ArcOfCircle CenterX=-1.5 CenterY=10 CenterZ=0 NormalX=0 NormalY=0 NormalZ=1 AngleXU=0 Radius=1.5 StartAngle=4.71239 EndAngle=7.85398
    g23: ArcOfCircle CenterX=-1.5 CenterY=15.75 CenterZ=0 NormalX=0 NormalY=0 NormalZ=1 AngleXU=0 Radius=1.5 StartAngle=4.71239 EndAngle=7.85398
    g24: LineSegment StartX=-49.19 StartY=69.25 StartZ=0 EndX=-1.5 EndY=69.25 EndZ=0
    g25: LineSegment StartX=-49.19 StartY=66.25 StartZ=0 EndX=-1.5 EndY=66.25 EndZ=0
    g26: LineSegment StartX=-49.19 StartY=63.5 StartZ=0 EndX=-1.5 EndY=63.5 EndZ=0
    g27: LineSegment StartX=-49.19 StartY=60.5 StartZ=0 EndX=-1.5 EndY=60.5 EndZ=0
    g28: LineSegment StartX=-49.19 StartY=57.75 StartZ=0 EndX=-1.5 EndY=57.75 EndZ=0
    g29: LineSegment StartX=-49.19 StartY=54.75 StartZ=0 EndX=-1.5 EndY=54.75 EndZ=0
    g30: LineSegment StartX=-49.19 StartY=52 StartZ=0 EndX=-11.49 EndY=52 EndZ=0
    g31: LineSegment StartX=-49.19 StartY=49 StartZ=0 EndX=-11.49 EndY=49 EndZ=0
    g32: LineSegment StartX=-49.19 StartY=46.25 StartZ=0 EndX=-16.28 EndY=46.25 EndZ=0
    g33: LineSegment StartX=-49.19 StartY=43.25 StartZ=0 EndX=-16.28 EndY=43.25 EndZ=0
    g34: LineSegment StartX=-49.19 StartY=40.5 StartZ=0 EndX=-18.2337 EndY=40.5 EndZ=0
    g35: LineSegment StartX=-49.19 StartY=37.5 StartZ=0 EndX=-18.23 EndY=37.5 EndZ=0
    g36: LineSegment StartX=-49.19 StartY=34.5 StartZ=0 EndX=-18.2337 EndY=34.5 EndZ=0
    g37: LineSegment StartX=-49.19 StartY=31.5 StartZ=0 EndX=-18.23 EndY=31.5 EndZ=0
    g38: LineSegment StartX=-49.19 StartY=28.75 StartZ=0 EndX=-16.2837 EndY=28.75 EndZ=0
    g39: LineSegment StartX=-49.19 StartY=25.75 StartZ=0 EndX=-16.28 EndY=25.75 EndZ=0
    g40: LineSegment StartX=-49.19 StartY=23 StartZ=0 EndX=-11.49 EndY=23 EndZ=0
    g41: LineSegment StartX=-49.19 StartY=20 StartZ=0 EndX=-11.49 EndY=20 EndZ=0
    g42: LineSegment StartX=-49.19 StartY=17.25 StartZ=0 EndX=-1.5 EndY=17.25 EndZ=0
    g43: LineSegment StartX=-49.19 StartY=14.25 StartZ=0 EndX=-1.5 EndY=14.25 EndZ=0
    g44: LineSegment StartX=-49.19 StartY=11.5 StartZ=0 EndX=-1.5 EndY=11.5 EndZ=0
    g45: LineSegment StartX=-49.19 StartY=8.5 StartZ=0 EndX=-1.5 EndY=8.5 EndZ=0
    g46: LineSegment StartX=-49.19 StartY=5.75 StartZ=0 EndX=-1.5 EndY=5.75 EndZ=0
    g47: LineSegment StartX=-49.19 StartY=2.75 StartZ=0 EndX=-1.5 EndY=2.75 EndZ=0
  constraints (120):
    c: Vertical(g0)
    c: Distance(g0) = 3
    c: Block(g0)
    c: Vertical(g1)
    c: Distance(g1) = 3
    c: Vertical(g2)
    c: Equal(g0,g2) = 3
    c: Block(g2)
    c: Vertical(g3)
    c: Equal(g1,g3) = 3
    c: Vertical(g4)
    c: Equal(g0,g4) = 3
    c: Block(g4)
    c: Vertical(g5)
    c: Equal(g1,g5) = 3
    c: Vertical(g6)
    c: Equal(g0,g6) = 3
    c: Block(g6)
    c: Vertical(g7)
    c: Equal(g1,g7) = 3
    c: Vertical(g8)
    c: Equal(g0,g8) = 3
    c: Block(g8)
    c: Vertical(g9)
    c: Equal(g1,g9) = 3
    c: Vertical(g10)
    c: Equal(g0,g10) = 3
    c: Block(g10)
    c: Vertical(g11)
    c: Equal(g1,g11) = 3
    c: Block(g12)
    c: Block(g13)
    c: Block(g14)
    c: Block(g15)
    c: Block(g16)
    c: Block(g17)
    c: Block(g18)
    c: Block(g19)
    c: Block(g20)
    c: Block(g21)
    c: Block(g22)
    c: Block(g23)
    c: Block(g11)
    c: Block(g9)
    c: Block(g7)
    c: Block(g5)
    c: Block(g3)
    c: Block(g1)
    c: Coincident(g24,g0)
    c: Coincident(g24,g12)
    c: Horizontal(g24)
    c: Coincident(g25,g0)
    c: Coincident(g25,g12)
    c: Horizontal(g25)
    c: Coincident(g26,g1)
    c: Coincident(g26,g13)
    c: Horizontal(g26)
    c: Coincident(g27,g1)
    c: Coincident(g27,g13)
    c: Horizontal(g27)
    c: Coincident(g28,g2)
    c: Coincident(g28,g14)
    c: Horizontal(g28)
    c: Coincident(g29,g2)
    c: Coincident(g29,g14)
    c: Horizontal(g29)
    c: Coincident(g30,g3)
    c: Coincident(g30,g15)
    c: Horizontal(g30)
    c: Coincident(g31,g3)
    c: Coincident(g31,g15)
    c: Horizontal(g31)
    c: Coincident(g32,g4)
    c: Coincident(g32,g16)
    c: Horizontal(g32)
    c: Coincident(g33,g4)
    c: Coincident(g33,g16)
    c: Horizontal(g33)
    c: Coincident(g34,g5)
    c: Coincident(g34,g17)
    c: Horizontal(g34)
    c: Coincident(g35,g5)
    c: Coincident(g35,g17)
    c: Horizontal(g35)
    c: Coincident(g36,g6)
    c: Coincident(g36,g19)
    c: Horizontal(g36)
    c: Coincident(g37,g6)
    c: Coincident(g37,g19)
    c: Horizontal(g37)
    c: Coincident(g38,g7)
    c: Coincident(g38,g18)
    c: Horizontal(g38)
    c: Coincident(g39,g7)
    c: Coincident(g39,g18)
    c: Horizontal(g39)
    c: Coincident(g40,g8)
    c: Coincident(g40,g20)
    c: Horizontal(g40)
    c: Coincident(g41,g8)
    c: Coincident(g41,g20)
    c: Horizontal(g41)
    c: Coincident(g42,g9)
    c: Coincident(g42,g23)
    c: Horizontal(g42)
    c: Coincident(g43,g9)
    c: Coincident(g43,g23)
    c: Horizontal(g43)
    c: Coincident(g44,g10)
    c: Coincident(g44,g22)
    c: Horizontal(g44)
    c: Coincident(g45,g10)
    c: Coincident(g45,g22)
    c: Horizontal(g45)
    c: Coincident(g46,g11)
    c: Coincident(g46,g21)
    c: Horizontal(g46)
    c: Coincident(g47,g11)
    c: Coincident(g47,g21)
    c: Horizontal(g47)
FEATURE [Sketcher::SketchObject] Sketch031
  FullyConstrained = true
  Placement = pos=(117,19,0) rot=(0.57735,0.57735,0.57735;2.0944rad)
  sketch-geometry (24):
    g0: ArcOfCircle CenterX=-49.19 CenterY=67.75 CenterZ=0 NormalX=0 NormalY=0 NormalZ=1 AngleXU=0 Radius=1.5 StartAngle=1.5708 EndAngle=4.71239
    g1: ArcOfCircle CenterX=-49.19 CenterY=62 CenterZ=0 NormalX=0 NormalY=0 NormalZ=1 AngleXU=0 Radius=1.5 StartAngle=1.5708 EndAngle=4.71239
    g2: ArcOfCircle CenterX=-49.19 CenterY=56.25 CenterZ=0 NormalX=0 NormalY=0 NormalZ=1 AngleXU=0 Radius=1.5 StartAngle=1.5708 EndAngle=4.71239
    g3: ArcOfCircle CenterX=-49.19 CenterY=50.5 CenterZ=0 NormalX=0 NormalY=0 NormalZ=1 AngleXU=0 Radius=1.5 StartAngle=1.5708 EndAngle=4.71239
    g4: ArcOfCircle CenterX=-49.19 CenterY=44.75 CenterZ=0 NormalX=0 NormalY=0 NormalZ=1 AngleXU=0 Radius=1.5 StartAngle=1.5708 EndAngle=4.71239
    g5: ArcOfCircle CenterX=-49.19 CenterY=39 CenterZ=0 NormalX=0 NormalY=0 NormalZ=1 AngleXU=0 Radius=1.5 StartAngle=1.5708 EndAngle=4.71239
    g6: ArcOfCircle CenterX=-49.19 CenterY=33 CenterZ=0 NormalX=0 NormalY=0 NormalZ=1 AngleXU=0 Radius=1.5 StartAngle=1.5708 EndAngle=4.71239
    g7: ArcOfCircle CenterX=-49.19 CenterY=27.25 CenterZ=0 NormalX=0 NormalY=0 NormalZ=1 AngleXU=0 Radius=1.5 StartAngle=1.5708 EndAngle=4.71239
    g8: ArcOfCircle CenterX=-49.19 CenterY=21.5 CenterZ=0 NormalX=0 NormalY=0 NormalZ=1 AngleXU=0 Radius=1.5 StartAngle=1.5708 EndAngle=4.71239
    g9: ArcOfCircle CenterX=-49.19 CenterY=15.75 CenterZ=0 NormalX=0 NormalY=0 NormalZ=1 AngleXU=0 Radius=1.5 StartAngle=1.5708 EndAngle=4.71239
    g10: ArcOfCircle CenterX=-49.19 CenterY=10 CenterZ=0 NormalX=0 NormalY=0 NormalZ=1 AngleXU=0 Radius=1.5 StartAngle=1.5708 EndAngle=4.71239
    g11: ArcOfCircle CenterX=-49.19 CenterY=4.25 CenterZ=0 NormalX=0 NormalY=0 NormalZ=1 AngleXU=0 Radius=1.5 StartAngle=1.5708 EndAngle=4.71239
    g12: LineSegment StartX=-49.19 StartY=69.25 StartZ=0 EndX=-49.19 EndY=66.25 EndZ=0
    g13: LineSegment StartX=-49.19 StartY=63.5 StartZ=0 EndX=-49.19 EndY=60.5 EndZ=0
    g14: LineSegment StartX=-49.19 StartY=57.75 StartZ=0 EndX=-49.19 EndY=54.75 EndZ=0
    g15: LineSegment StartX=-49.19 StartY=52 StartZ=0 EndX=-49.19 EndY=49 EndZ=0
    g16: LineSegment StartX=-49.19 StartY=46.25 StartZ=0 EndX=-49.19 EndY=43.25 EndZ=0
    g17: LineSegment StartX=-49.19 StartY=40.5 StartZ=0 EndX=-49.19 EndY=37.5 EndZ=0
    g18: LineSegment StartX=-49.19 StartY=34.5 StartZ=0 EndX=-49.19 EndY=31.5 EndZ=0
    g19: LineSegment StartX=-49.19 StartY=28.75 StartZ=0 EndX=-49.19 EndY=25.75 EndZ=0
    g20: LineSegment StartX=-49.19 StartY=23 StartZ=0 EndX=-49.19 EndY=20 EndZ=0
    g21: LineSegment StartX=-49.19 StartY=17.25 StartZ=0 EndX=-49.19 EndY=14.25 EndZ=0
    g22: LineSegment StartX=-49.19 StartY=11.5 StartZ=0 EndX=-49.19 EndY=8.5 EndZ=0
    g23: LineSegment StartX=-49.19 StartY=5.75 StartZ=0 EndX=-49.19 EndY=2.75 EndZ=0
  constraints (48):
    c: Block(g0)
    c: Block(g1)
    c: Block(g2)
    c: Block(g3)
    c: Block(g4)
    c: Block(g5)
    c: Block(g6)
    c: Block(g7)
    c: Block(g8)
    c: Block(g9)
    c: Block(g10)
    c: Block(g11)
    c: Coincident(g12,g0)
    c: Coincident(g12,g0)
    c: Vertical(g12)
    c: Vertical(g13)
    c: Coincident(g13,g1)
    c: Vertical(g14)
    c: Coincident(g14,g2)
    c: Vertical(g15)
    c: Coincident(g15,g3)
    c: Vertical(g16)
    c: Coincident(g16,g4)
    c: Vertical(g17)
    c: Coincident(g17,g5)
    c: Vertical(g18)
    c: Coincident(g18,g6)
    c: Vertical(g19)
    c: Coincident(g19,g7)
    c: Vertical(g20)
    c: Coincident(g20,g8)
    c: Vertical(g21)
    c: Coincident(g21,g9)
    c: Vertical(g22)
    c: Coincident(g22,g10)
    c: Vertical(g23)
    c: Coincident(g23,g11)
    c: Block(g23)
    c: Block(g22)
    c: Block(g21)
    c: Block(g20)
    c: Block(g13)
    c: Block(g14)
    c: Block(g15)
    c: Block(g16)
    c: Block(g17)
    c: Block(g18)
    c: Block(g19)
FEATURE [Part::Extrusion] Extrude022
  Base = -> Sketch030
  Dir = (1,-2e-16,2e-16)
  DirMode = 2
  FaceMakerClass = Part::FaceMakerBullseye
  LengthFwd = 19
  LengthRev = 0
  Placement = pos=(-19,0,0) rot=(0,0,1;0rad)
  Solid = true
  Symmetric = false
FEATURE [Part::Fillet] Fillet022
  Base = -> Extrude022
  Edges = 24 edges r=1.49: [Edge6,Edge11,Edge18,Edge23,Edge30,Edge35,Edge42,Edge47,Edge54,Edge59,Edge66,Edge71,Edge78,Edge83,Edge90,Edge95,Edge102,Edge107,Edge114,Edge119,Edge126,Edge131,Edge138,Edge143]
FEATURE [Part::Cut] Cut020  label="top010"
  Base = -> Cut019
  Tool = -> Fillet022
FEATURE [Sketcher::SketchObject] Sketch032
  FullyConstrained = true
  Placement = pos=(117,19,0) rot=(0.57735,0.57735,0.57735;2.0944rad)
  sketch-geometry (48):
    g0: LineSegment StartX=-49.19 StartY=69.25 StartZ=0 EndX=-49.19 EndY=66.25 EndZ=0
    g1: LineSegment StartX=-49.19 StartY=63.5 StartZ=0 EndX=-49.19 EndY=60.5 EndZ=0
    g2: LineSegment StartX=-49.19 StartY=57.75 StartZ=0 EndX=-49.19 EndY=54.75 EndZ=0
    g3: LineSegment StartX=-49.19 StartY=52 StartZ=0 EndX=-49.19 EndY=49 EndZ=0
    g4: LineSegment StartX=-49.19 StartY=46.25 StartZ=0 EndX=-49.19 EndY=43.25 EndZ=0
    g5: LineSegment StartX=-49.19 StartY=40.5 StartZ=0 EndX=-49.19 EndY=37.5 EndZ=0
    g6: LineSegment StartX=-49.19 StartY=34.5 StartZ=0 EndX=-49.19 EndY=31.5 EndZ=0
    g7: LineSegment StartX=-49.19 StartY=28.75 StartZ=0 EndX=-49.19 EndY=25.75 EndZ=0
    g8: LineSegment StartX=-49.19 StartY=23 StartZ=0 EndX=-49.19 EndY=20 EndZ=0
    g9: LineSegment StartX=-49.19 StartY=17.25 StartZ=0 EndX=-49.19 EndY=14.25 EndZ=0
    g10: LineSegment StartX=-49.19 StartY=11.5 StartZ=0 EndX=-49.19 EndY=8.5 EndZ=0
    g11: LineSegment StartX=-49.19 StartY=5.75 StartZ=0 EndX=-49.19 EndY=2.75 EndZ=0
    g12: ArcOfCircle CenterX=-1.5 CenterY=67.75 CenterZ=0 NormalX=0 NormalY=0 NormalZ=1 AngleXU=0 Radius=1.5 StartAngle=4.71239 EndAngle=7.85398
    g13: ArcOfCircle CenterX=-1.5 CenterY=62 CenterZ=0 NormalX=0 NormalY=0 NormalZ=1 AngleXU=0 Radius=1.5 StartAngle=4.71239 EndAngle=7.85398
    g14: ArcOfCircle CenterX=-1.5 CenterY=56.25 CenterZ=0 NormalX=0 NormalY=0 NormalZ=1 AngleXU=0 Radius=1.5 StartAngle=4.71239 EndAngle=7.85398
    g15: ArcOfCircle CenterX=-11.49 CenterY=50.5 CenterZ=0 NormalX=0 NormalY=0 NormalZ=1 AngleXU=0 Radius=1.5 StartAngle=4.71239 EndAngle=7.85398
    g16: ArcOfCircle CenterX=-16.28 CenterY=44.75 CenterZ=0 NormalX=0 NormalY=0 NormalZ=1 AngleXU=0 Radius=1.5 StartAngle=4.71239 EndAngle=7.85398
    g17: ArcOfCircle CenterX=-18.2337 CenterY=39 CenterZ=0 NormalX=0 NormalY=0 NormalZ=1 AngleXU=0 Radius=1.5 StartAngle=4.71485 EndAngle=7.85398
    g18: ArcOfCircle CenterX=-16.2837 CenterY=27.25 CenterZ=0 NormalX=0 NormalY=0 NormalZ=1 AngleXU=0 Radius=1.5 StartAngle=4.71485 EndAngle=7.85398
    g19: ArcOfCircle CenterX=-18.2337 CenterY=33 CenterZ=0 NormalX=0 NormalY=0 NormalZ=1 AngleXU=0 Radius=1.5 StartAngle=4.71485 EndAngle=7.85398
    g20: ArcOfCircle CenterX=-11.49 CenterY=21.5 CenterZ=0 NormalX=0 NormalY=0 NormalZ=1 AngleXU=0 Radius=1.5 StartAngle=4.71239 EndAngle=7.85398
    g21: ArcOfCircle CenterX=-1.5 CenterY=4.25 CenterZ=0 NormalX=0 NormalY=0 NormalZ=1 AngleXU=0 Radius=1.5 StartAngle=4.71239 EndAngle=7.85398
    g22: ArcOfCircle CenterX=-1.5 CenterY=10 CenterZ=0 NormalX=0 NormalY=0 NormalZ=1 AngleXU=0 Radius=1.5 StartAngle=4.71239 EndAngle=7.85398
    g23: ArcOfCircle CenterX=-1.5 CenterY=15.75 CenterZ=0 NormalX=0 NormalY=0 NormalZ=1 AngleXU=0 Radius=1.5 StartAngle=4.71239 EndAngle=7.85398
    g24: LineSegment StartX=-49.19 StartY=69.25 StartZ=0 EndX=-1.5 EndY=69.25 EndZ=0
    g25: LineSegment StartX=-49.19 StartY=66.25 StartZ=0 EndX=-1.5 EndY=66.25 EndZ=0
    g26: LineSegment StartX=-49.19 StartY=63.5 StartZ=0 EndX=-1.5 EndY=63.5 EndZ=0
    g27: LineSegment StartX=-49.19 StartY=60.5 StartZ=0 EndX=-1.5 EndY=60.5 EndZ=0
    g28: LineSegment StartX=-49.19 StartY=57.75 StartZ=0 EndX=-1.5 EndY=57.75 EndZ=0
    g29: LineSegment StartX=-49.19 StartY=54.75 StartZ=0 EndX=-1.5 EndY=54.75 EndZ=0
    g30: LineSegment StartX=-49.19 StartY=52 StartZ=0 EndX=-11.49 EndY=52 EndZ=0
    g31: LineSegment StartX=-49.19 StartY=49 StartZ=0 EndX=-11.49 EndY=49 EndZ=0
    g32: LineSegment StartX=-49.19 StartY=46.25 StartZ=0 EndX=-16.28 EndY=46.25 EndZ=0
    g33: LineSegment StartX=-49.19 StartY=43.25 StartZ=0 EndX=-16.28 EndY=43.25 EndZ=0
    g34: LineSegment StartX=-49.19 StartY=40.5 StartZ=0 EndX=-18.2337 EndY=40.5 EndZ=0
    g35: LineSegment StartX=-49.19 StartY=37.5 StartZ=0 EndX=-18.23 EndY=37.5 EndZ=0
    g36: LineSegment StartX=-49.19 StartY=34.5 StartZ=0 EndX=-18.2337 EndY=34.5 EndZ=0
    g37: LineSegment StartX=-49.19 StartY=31.5 StartZ=0 EndX=-18.23 EndY=31.5 EndZ=0
    g38: LineSegment StartX=-49.19 StartY=28.75 StartZ=0 EndX=-16.2837 EndY=28.75 EndZ=0
    g39: LineSegment StartX=-49.19 StartY=25.75 StartZ=0 EndX=-16.28 EndY=25.75 EndZ=0
    g40: LineSegment StartX=-49.19 StartY=23 StartZ=0 EndX=-11.49 EndY=23 EndZ=0
    g41: LineSegment StartX=-49.19 StartY=20 StartZ=0 EndX=-11.49 EndY=20 EndZ=0
    g42: LineSegment StartX=-49.19 StartY=17.25 StartZ=0 EndX=-1.5 EndY=17.25 EndZ=0
    g43: LineSegment StartX=-49.19 StartY=14.25 StartZ=0 EndX=-1.5 EndY=14.25 EndZ=0
    g44: LineSegment StartX=-49.19 StartY=11.5 StartZ=0 EndX=-1.5 EndY=11.5 EndZ=0
    g45: LineSegment StartX=-49.19 StartY=8.5 StartZ=0 EndX=-1.5 EndY=8.5 EndZ=0
    g46: LineSegment StartX=-49.19 StartY=5.75 StartZ=0 EndX=-1.5 EndY=5.75 EndZ=0
    g47: LineSegment StartX=-49.19 StartY=2.75 StartZ=0 EndX=-1.5 EndY=2.75 EndZ=0
  constraints (120):
    c: Vertical(g0)
    c: Distance(g0) = 3
    c: Block(g0)
    c: Vertical(g1)
    c: Distance(g1) = 3
    c: Vertical(g2)
    c: Equal(g0,g2) = 3
    c: Block(g2)
    c: Vertical(g3)
    c: Equal(g1,g3) = 3
    c: Vertical(g4)
    c: Equal(g0,g4) = 3
    c: Block(g4)
    c: Vertical(g5)
    c: Equal(g1,g5) = 3
    c: Vertical(g6)
    c: Equal(g0,g6) = 3
    c: Block(g6)
    c: Vertical(g7)
    c: Equal(g1,g7) = 3
    c: Vertical(g8)
    c: Equal(g0,g8) = 3
    c: Block(g8)
    c: Vertical(g9)
    c: Equal(g1,g9) = 3
    c: Vertical(g10)
    c: Equal(g0,g10) = 3
    c: Block(g10)
    c: Vertical(g11)
    c: Equal(g1,g11) = 3
    c: Block(g12)
    c: Block(g13)
    c: Block(g14)
    c: Block(g15)
    c: Block(g16)
    c: Block(g17)
    c: Block(g18)
    c: Block(g19)
    c: Block(g20)
    c: Block(g21)
    c: Block(g22)
    c: Block(g23)
    c: Block(g11)
    c: Block(g9)
    c: Block(g7)
    c: Block(g5)
    c: Block(g3)
    c: Block(g1)
    c: Coincident(g24,g0)
    c: Coincident(g24,g12)
    c: Horizontal(g24)
    c: Coincident(g25,g0)
    c: Coincident(g25,g12)
    c: Horizontal(g25)
    c: Coincident(g26,g1)
    c: Coincident(g26,g13)
    c: Horizontal(g26)
    c: Coincident(g27,g1)
    c: Coincident(g27,g13)
    c: Horizontal(g27)
    c: Coincident(g28,g2)
    c: Coincident(g28,g14)
    c: Horizontal(g28)
    c: Coincident(g29,g2)
    c: Coincident(g29,g14)
    c: Horizontal(g29)
    c: Coincident(g30,g3)
    c: Coincident(g30,g15)
    c: Horizontal(g30)
    c: Coincident(g31,g3)
    c: Coincident(g31,g15)
    c: Horizontal(g31)
    c: Coincident(g32,g4)
    c: Coincident(g32,g16)
    c: Horizontal(g32)
    c: Coincident(g33,g4)
    c: Coincident(g33,g16)
    c: Horizontal(g33)
    c: Coincident(g34,g5)
    c: Coincident(g34,g17)
    c: Horizontal(g34)
    c: Coincident(g35,g5)
    c: Coincident(g35,g17)
    c: Horizontal(g35)
    c: Coincident(g36,g6)
    c: Coincident(g36,g19)
    c: Horizontal(g36)
    c: Coincident(g37,g6)
    c: Coincident(g37,g19)
    c: Horizontal(g37)
    c: Coincident(g38,g7)
    c: Coincident(g38,g18)
    c: Horizontal(g38)
    c: Coincident(g39,g7)
    c: Coincident(g39,g18)
    c: Horizontal(g39)
    c: Coincident(g40,g8)
    c: Coincident(g40,g20)
    c: Horizontal(g40)
    c: Coincident(g41,g8)
    c: Coincident(g41,g20)
    c: Horizontal(g41)
    c: Coincident(g42,g9)
    c: Coincident(g42,g23)
    c: Horizontal(g42)
    c: Coincident(g43,g9)
    c: Coincident(g43,g23)
    c: Horizontal(g43)
    c: Coincident(g44,g10)
    c: Coincident(g44,g22)
    c: Horizontal(g44)
    c: Coincident(g45,g10)
    c: Coincident(g45,g22)
    c: Horizontal(g45)
    c: Coincident(g46,g11)
    c: Coincident(g46,g21)
    c: Horizontal(g46)
    c: Coincident(g47,g11)
    c: Coincident(g47,g21)
    c: Horizontal(g47)
FEATURE [Part::Extrusion] Extrude023
  Base = -> Sketch032
  Dir = (1,-2e-16,2e-16)
  DirMode = 2
  FaceMakerClass = Part::FaceMakerBullseye
  LengthFwd = 19
  LengthRev = 0
  Placement = pos=(-19,0,0) rot=(0,0,1;0rad)
  Solid = true
  Symmetric = false
FEATURE [Part::Fillet] Fillet023
  Base = -> Extrude023
  Edges = 24 edges r=1.49: [Edge6,Edge11,Edge18,Edge23,Edge30,Edge35,Edge42,Edge47,Edge54,Edge59,Edge66,Edge71,Edge78,Edge83,Edge90,Edge95,Edge102,Edge107,Edge114,Edge119,Edge126,Edge131,Edge138,Edge143]
  Placement = pos=(0,0.05,0) rot=(0,0,1;0rad)
FEATURE [Part::Cut] Cut014  label="bottom003"
  Base = -> Cut007
  Tool = -> Fusion047
FEATURE [Part::Cut] Cut021  label="bottom004"
  Base = -> Cut014
  Tool = -> Fillet023
FEATURE [Sketcher::SketchObject] Sketch033
  FullyConstrained = true
  Placement = pos=(117,19,0) rot=(0.57735,0.57735,0.57735;2.0944rad)
  sketch-geometry (8):
    g0: LineSegment StartX=-49.19 StartY=69.25 StartZ=0 EndX=-49.19 EndY=66.25 EndZ=0
    g1: LineSegment StartX=-49.19 StartY=5.75 StartZ=0 EndX=-49.19 EndY=2.75 EndZ=0
    g2: ArcOfCircle CenterX=-1.5 CenterY=67.75 CenterZ=0 NormalX=0 NormalY=0 NormalZ=1 AngleXU=0 Radius=1.5 StartAngle=4.71239 EndAngle=7.85398
    g3: ArcOfCircle CenterX=-1.5 CenterY=4.25 CenterZ=0 NormalX=0 NormalY=0 NormalZ=1 AngleXU=0 Radius=1.5 StartAngle=4.71239 EndAngle=7.85398
    g4: LineSegment StartX=-49.19 StartY=69.25 StartZ=0 EndX=-1.5 EndY=69.25 EndZ=0
    g5: LineSegment StartX=-49.19 StartY=66.25 StartZ=0 EndX=-1.5 EndY=66.25 EndZ=0
    g6: LineSegment StartX=-49.19 StartY=5.75 StartZ=0 EndX=-1.5 EndY=5.75 EndZ=0
    g7: LineSegment StartX=-49.19 StartY=2.75 StartZ=0 EndX=-1.5 EndY=2.75 EndZ=0
  constraints (19):
    c: Vertical(g0)
    c: Distance(g0) = 3
    c: Block(g0)
    c: Vertical(g1)
    c: Block(g2)
    c: Block(g3)
    c: Block(g1)
    c: Coincident(g4,g0)
    c: Coincident(g4,g2)
    c: Horizontal(g4)
    c: Coincident(g5,g0)
    c: Coincident(g5,g2)
    c: Horizontal(g5)
    c: Coincident(g6,g1)
    c: Coincident(g6,g3)
    c: Horizontal(g6)
    c: Coincident(g7,g1)
    c: Coincident(g7,g3)
    c: Horizontal(g7)
FEATURE [Sketcher::SketchObject] Sketch034
  FullyConstrained = true
  Placement = pos=(117,19,0) rot=(0.57735,0.57735,0.57735;2.0944rad)
  sketch-geometry (8):
    g0: LineSegment StartX=-49.19 StartY=63.5 StartZ=0 EndX=-49.19 EndY=60.5 EndZ=0
    g1: LineSegment StartX=-49.19 StartY=11.5 StartZ=0 EndX=-49.19 EndY=8.5 EndZ=0
    g2: ArcOfCircle CenterX=-1.5 CenterY=62 CenterZ=0 NormalX=0 NormalY=0 NormalZ=1 AngleXU=0 Radius=1.5 StartAngle=4.71239 EndAngle=7.85398
    g3: ArcOfCircle CenterX=-1.5 CenterY=10 CenterZ=0 NormalX=0 NormalY=0 NormalZ=1 AngleXU=0 Radius=1.5 StartAngle=4.71239 EndAngle=7.85398
    g4: LineSegment StartX=-49.19 StartY=63.5 StartZ=0 EndX=-1.5 EndY=63.5 EndZ=0
    g5: LineSegment StartX=-49.19 StartY=60.5 StartZ=0 EndX=-1.5 EndY=60.5 EndZ=0
    g6: LineSegment StartX=-49.19 StartY=11.5 StartZ=0 EndX=-1.5 EndY=11.5 EndZ=0
    g7: LineSegment StartX=-49.19 StartY=8.5 StartZ=0 EndX=-1.5 EndY=8.5 EndZ=0
  constraints (19):
    c: Vertical(g0)
    c: Distance(g0) = 3
    c: Vertical(g1)
    c: Block(g1)
    c: Block(g2)
    c: Block(g3)
    c: Block(g0)
    c: Coincident(g4,g0)
    c: Coincident(g4,g2)
    c: Horizontal(g4)
    c: Coincident(g5,g0)
    c: Coincident(g5,g2)
    c: Horizontal(g5)
    c: Coincident(g6,g1)
    c: Coincident(g6,g3)
    c: Horizontal(g6)
    c: Coincident(g7,g1)
    c: Coincident(g7,g3)
    c: Horizontal(g7)
FEATURE [Part::Extrusion] Extrude024
  Base = -> Sketch033
  Dir = (1,0,0)
  DirMode = 2
  FaceMakerClass = Part::FaceMakerBullseye
  LengthFwd = 10
  LengthRev = 0
  Solid = true
  Symmetric = false
FEATURE [Part::Extrusion] Extrude025
  Base = -> Sketch034
  Dir = (1,0,0)
  DirMode = 2
  FaceMakerClass = Part::FaceMakerBullseye
  LengthFwd = 10
  LengthRev = 0
  Solid = true
  Symmetric = false
FEATURE [Part::Fillet] Fillet024  label="removeFromtMoreFrontCaseScrewRetainers"
  Base = -> Extrude024
  Edges = 4 edges r=1.49: [Edge6,Edge11,Edge18,Edge23]
  Placement = pos=(-11,0,0) rot=(0,0,1;0rad)
FEATURE [Part::Fillet] Fillet025  label="removeFromtMoreFrontCaseScrewRetainers001"
  Base = -> Extrude025
  Edges = 4 edges r=1.49: [Edge6,Edge11,Edge18,Edge23]
  Placement = pos=(-19,0,0) rot=(0,0,1;0rad)
FEATURE [Part::Cut] Cut022
  Base = -> Cut015
  Tool = -> Fillet025
FEATURE [Part::Cut] Cut023  label="screwRetainers"
  Base = -> Cut022
  Tool = -> Fillet024
FEATURE [Part::MultiFuse] Fusion056  label="bottom005"
  Shapes = -> [Fusion044,Cut021]
FEATURE [Part::MultiFuse] Fusion057  label="casePillars001"
  Shapes = -> [Cut016,Fusion052]
FEATURE [Part::MultiFuse] Fusion058  label="bottom006"
  Shapes = -> [Fusion056,Cut023]
FEATURE [Part::MultiFuse] Fusion059  label="bottom007"
  Shapes = -> [Fusion058,Fillet005]
FEATURE [Part::MultiFuse] Fusion060  label="bottom008"
  Shapes = -> [Fusion059,Fusion]
FEATURE [Part::MultiFuse] Fusion061  label="top011"
  Shapes = -> [Cut006,Cut020]
FEATURE [Part::MultiFuse] Fusion062  label="top012"
  Shapes = -> [Fusion057,Fusion061]
FEATURE [Sketcher::SketchObject] Sketch035  label="topSketch007"
  FullyConstrained = true
  sketch-geometry (6):
    g0: LineSegment StartX=19 StartY=38 StartZ=0 EndX=117 EndY=38 EndZ=0
    g1: ArcOfCircle CenterX=19 CenterY=19 CenterZ=0 NormalX=0 NormalY=0 NormalZ=1 AngleXU=0 Radius=19 StartAngle=1.5708 EndAngle=3.14159
    g2: LineSegment StartX=117 StartY=38 StartZ=0 EndX=117 EndY=19 EndZ=0
    g3: LineSegment StartX=98 StartY=1.0161e-12 StartZ=0 EndX=5.22862e-06 EndY=1.0161e-12 EndZ=0
    g4: LineSegment StartX=5.22862e-06 StartY=19 StartZ=0 EndX=5.22862e-06 EndY=1.0161e-12 EndZ=0
    g5: ArcOfCircle CenterX=98 CenterY=19 CenterZ=0 NormalX=0 NormalY=0 NormalZ=1 AngleXU=0 Radius=19 StartAngle=4.71239 EndAngle=6.28319
  constraints (16):
    c: Horizontal(g0)
    c: Distance(g0) = 98
    c: Coincident(g1,g0)
    c: Block(g1)
    c: Coincident(g2,g0)
    c: Vertical(g2)
    c: Distance(g2) = 19
    c: Horizontal(g3)
    c: Coincident(g4,g1)
    c: Vertical(g4)
    c: Coincident(g3,g4)
    c: Block(g3)
    c: Coincident(g5,g2)
    c: Coincident(g5,g3)
    c: Block(g0)
    c: Block(g5)
FEATURE [Part::Extrusion] Extrude026  label="sideA001"
  Base = -> Sketch035
  Dir = (0,0,1)
  DirMode = 2
  FaceMakerClass = Part::FaceMakerBullseye
  LengthFwd = 3
  LengthRev = 0
  Placement = pos=(0,0,-2.7) rot=(0,0,1;0rad)
  Solid = true
  Symmetric = false
FEATURE [Sketcher::SketchObject] Sketch036  label="topSketch008"
  FullyConstrained = true
  sketch-geometry (6):
    g0: LineSegment StartX=19 StartY=38 StartZ=0 EndX=117 EndY=38 EndZ=0
    g1: ArcOfCircle CenterX=19 CenterY=19 CenterZ=0 NormalX=0 NormalY=0 NormalZ=1 AngleXU=0 Radius=19 StartAngle=1.5708 EndAngle=3.14159
    g2: LineSegment StartX=117 StartY=38 StartZ=0 EndX=117 EndY=19 EndZ=0
    g3: LineSegment StartX=98 StartY=1.0161e-12 StartZ=0 EndX=5.22862e-06 EndY=1.0161e-12 EndZ=0
    g4: LineSegment StartX=5.22862e-06 StartY=19 StartZ=0 EndX=5.22862e-06 EndY=1.0161e-12 EndZ=0
    g5: ArcOfCircle CenterX=98 CenterY=19 CenterZ=0 NormalX=0 NormalY=0 NormalZ=1 AngleXU=0 Radius=19 StartAngle=4.71239 EndAngle=6.28319
  constraints (16):
    c: Horizontal(g0)
    c: Distance(g0) = 98
    c: Coincident(g1,g0)
    c: Block(g1)
    c: Coincident(g2,g0)
    c: Vertical(g2)
    c: Distance(g2) = 19
    c: Horizontal(g3)
    c: Coincident(g4,g1)
    c: Vertical(g4)
    c: Coincident(g3,g4)
    c: Block(g3)
    c: Coincident(g5,g2)
    c: Coincident(g5,g3)
    c: Block(g0)
    c: Block(g5)
FEATURE [Part::Extrusion] Extrude027  label="sideB001"
  Base = -> Sketch036
  Dir = (0,0,1)
  DirMode = 2
  FaceMakerClass = Part::FaceMakerBullseye
  LengthFwd = 3
  LengthRev = 0
  Placement = pos=(0,0,71.7) rot=(0,0,1;0rad)
  Solid = true
  Symmetric = false
FEATURE [Part::MultiFuse] Fusion064  label="removeFromBottom"
  Shapes = -> [Extrude026,Extrude027]
FEATURE [Part::Cut] Cut024  label="bottom009"
  Base = -> Fusion060
  Tool = -> Fusion064
FEATURE [Sketcher::SketchObject] Sketch037  label="topSketch009"
  FullyConstrained = true
  sketch-geometry (6):
    g0: ArcOfCircle CenterX=19 CenterY=19 CenterZ=0 NormalX=0 NormalY=0 NormalZ=1 AngleXU=0 Radius=19 StartAngle=1.5708 EndAngle=3.14159
    g1: LineSegment StartX=5.22862e-06 StartY=19 StartZ=0 EndX=5.22862e-06 EndY=1.19904e-11 EndZ=0
    g2: LineSegment StartX=19 StartY=38 StartZ=0 EndX=124 EndY=38 EndZ=0
    g3: LineSegment StartX=5.22862e-06 StartY=1.19904e-11 StartZ=0 EndX=105 EndY=1.19904e-11 EndZ=0
    g4: ArcOfCircle CenterX=105 CenterY=19 CenterZ=0 NormalX=0 NormalY=0 NormalZ=1 AngleXU=0 Radius=19 StartAngle=4.71239 EndAngle=6.28319
    g5: LineSegment StartX=124 StartY=38 StartZ=0 EndX=124 EndY=19 EndZ=0
  constraints (16):
    c: Block(g0)
    c: Coincident(g1,g0)
    c: Vertical(g1)
    c: Horizontal(g2)
    c: Distance(g2) = 105
    c: Coincident(g2,g0)
    c: Distance(g1) = 19
    c: Coincident(g3,g1)
    c: Horizontal(g3)
    c: Distance(g3) = 105
    c: Block(g4)
    c: Coincident(g4,g3)
    c: Coincident(g5,g2)
    c: Coincident(g5,g4)
    c: Vertical(g5)
    c: Distance(g5) = 19
FEATURE [Part::Extrusion] Extrude028  label="sideB"
  Base = -> Sketch037
  Dir = (0,0,1)
  DirMode = 2
  FaceMakerClass = Part::FaceMakerBullseye
  LengthFwd = 3
  LengthRev = 0
  Placement = pos=(0,0,72) rot=(0,0,1;0rad)
  Solid = true
  Symmetric = false
FEATURE [Sketcher::SketchObject] Sketch038  label="topSketch010"
  FullyConstrained = true
  sketch-geometry (20):
    g0: LineSegment StartX=5.21097e-06 StartY=3 StartZ=0 EndX=5.21097e-06 EndY=19 EndZ=0
    g1: ArcOfCircle CenterX=19 CenterY=19 CenterZ=0 NormalX=0 NormalY=0 NormalZ=1 AngleXU=0 Radius=19 StartAngle=1.5708 EndAngle=3.14159
    g2: ArcOfCircle CenterX=19 CenterY=19 CenterZ=0 NormalX=0 NormalY=0 NormalZ=1 AngleXU=0 Radius=16 StartAngle=1.5708 EndAngle=3.14159
    g3: LineSegment StartX=114 StartY=35 StartZ=0 EndX=19 EndY=35 EndZ=0
    g4: LineSegment StartX=5.21097e-06 StartY=3 StartZ=0 EndX=5.21097e-06 EndY=0 EndZ=0
    g5: LineSegment StartX=3 StartY=0 StartZ=0 EndX=5.21097e-06 EndY=0 EndZ=0
    g6: LineSegment StartX=3 StartY=19 StartZ=0 EndX=3 EndY=0 EndZ=0
    g7: LineSegment StartX=19 StartY=38 StartZ=0 EndX=124 EndY=38 EndZ=0
    g8: Circle CenterX=119 CenterY=35 CenterZ=0 NormalX=0 NormalY=0 NormalZ=1 AngleXU=0 Radius=1
    g9: Circle CenterX=121 CenterY=35 CenterZ=0 NormalX=0 NormalY=0 NormalZ=1 AngleXU=0 Radius=1
    g10: Circle CenterX=121 CenterY=33 CenterZ=0 NormalX=0 NormalY=0 NormalZ=1 AngleXU=0 Radius=1
    g11: BSplineCurve PolesCount=3 KnotsCount=2 Degree=2 IsPeriodic=0
    g12: GeomPoint X=119 Y=35 Z=0
    g13: GeomPoint X=121 Y=33 Z=0
    g14: LineSegment StartX=119 StartY=35 StartZ=0 EndX=114 EndY=35 EndZ=0
    g15: ArcOfCircle CenterX=105 CenterY=19 CenterZ=0 NormalX=0 NormalY=0 NormalZ=1 AngleXU=0 Radius=19 StartAngle=5.7297 EndAngle=6.28319
    g16: ArcOfCircle CenterX=105 CenterY=19 CenterZ=0 NormalX=0 NormalY=0 NormalZ=1 AngleXU=0 Radius=16 StartAngle=5.60905 EndAngle=6.28319
    g17: LineSegment StartX=121 StartY=33 StartZ=0 EndX=121 EndY=19 EndZ=0
    g18: LineSegment StartX=124 StartY=38 StartZ=0 EndX=124 EndY=19 EndZ=0
    g19: LineSegment StartX=117.5 StartY=9.01251 StartZ=0 EndX=121.163 EndY=9.0125 EndZ=0
  constraints (46):
    c: Vertical(g0)
    c: Block(g0)
    c: Coincident(g1,g0)
    c: Block(g1)
    c: Coincident(g2,g1)
    c: Block(g2)
    c: Coincident(g3,g2)
    c: Horizontal(g3)
    c: Tangent(g3,g2)
    c: Coincident(g4,g0)
    c: Distance(g4) = 3
    c: Vertical(g4)
    c: Coincident(g5,g4)
    c: Horizontal(g5)
    c: Coincident(g6,g2)
    c: Coincident(g6,g5)
    c: Vertical(g6)
    c: Horizontal(g7)
    c: Distance(g7) = 105
    c: Coincident(g7,g1)
    c: Block(g3)
    c: Weight(g8) = 1
    c: Equal(g8,g9)
    c: Equal(g8,g10)
    c: InternalAlignment(g8,g11)
    c: InternalAlignment(g9,g11)
    c: InternalAlignment(g10,g11)
    c: InternalAlignment(g12,g11)
    c: InternalAlignment(g13,g11)
    c: Block(g11)
    c: Coincident(g14,g11)
    c: Coincident(g14,g3)
    c: Horizontal(g14)
    c: Block(g15)
    c: Coincident(g16,g15)
    c: Block(g16)
    c: Coincident(g17,g11)
    c: Coincident(g17,g16)
    c: Vertical(g17)
    c: Distance(g17) = 14
    c: Coincident(g18,g7)
    c: Coincident(g18,g15)
    c: Vertical(g18)
    c: Distance(g18) = 19
    c: Coincident(g19,g16)
    c: Coincident(g19,g15)
FEATURE [Part::Extrusion] Extrude029
  Base = -> Sketch038
  Dir = (0,0,1)
  DirMode = 2
  FaceMakerClass = Part::FaceMakerBullseye
  LengthFwd = 72
  LengthRev = 0
  Solid = true
  Symmetric = false
FEATURE [Part::Chamfer] Chamfer
  Base = -> Extrude029
  Edges = 1 edges r=2.7: [Edge35]
FEATURE [Part::Chamfer] Chamfer001
  Base = -> Chamfer
  Edges = 1 edges r=1.8: [Edge21]
